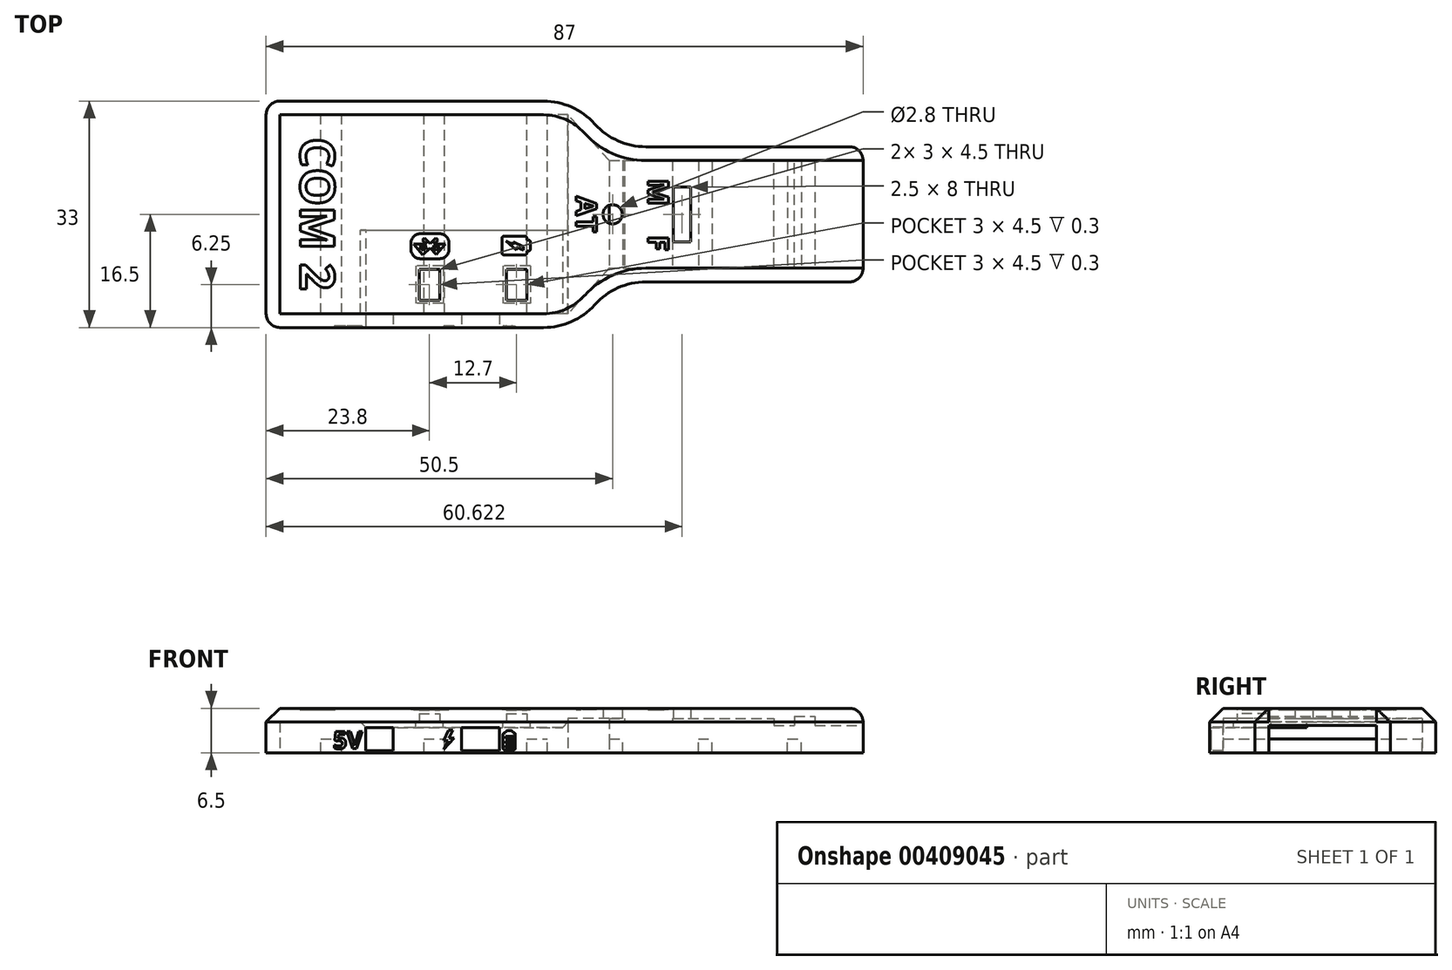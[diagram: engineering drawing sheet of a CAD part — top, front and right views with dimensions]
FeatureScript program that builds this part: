
annotation { "Feature Type Name" : "Feature", "Feature Type Description" : "" }
export const myFeature = defineFeature(function(context is Context, id is Id, definition is map)
    precondition{}
    {
        {
            var Q0;
            Q0=qCreatedBy(makeId("Top.planeOp"),FACE);
            var sketch = newSketch(context, id + "F0", { "sketchPlane" : qUnion([Q0])});
            skLineSegment(sketch, "E0.bottom", {"start": v(0, 14.5) * mm, "end": v(-42, 14.5) * mm});
            skLineSegment(sketch, "E0.top", {"start": v(0, -14.5) * mm, "end": v(-42, -14.5) * mm});
            skLineSegment(sketch, "E0.left", {"start": v(0, 14.5) * mm, "end": v(0, -14.5) * mm});
            skLineSegment(sketch, "E0.right", {"start": v(-42, 14.5) * mm, "end": v(-42, -14.5) * mm});
            skLineSegment(sketch, "E1.bottom", {"start": v(6, 7.85) * mm, "end": v(41, 7.85) * mm});
            skLineSegment(sketch, "E1.top", {"start": v(6, -7.85) * mm, "end": v(41, -7.85) * mm});
            skLineSegment(sketch, "E1.left", {"start": v(6, 7.85) * mm, "end": v(6, -7.85) * mm});
            skLineSegment(sketch, "E1.right", {"start": v(41, 7.85) * mm, "end": v(41, -7.85) * mm});
            skLineSegment(sketch, "E2", {"start": v(6, 7.85) * mm, "end": v(0, 14.5) * mm});
            skLineSegment(sketch, "E3", {"start": v(6, -7.85) * mm, "end": v(0, -14.5) * mm});
            skCircle(sketch, "E4", {"center": v(6.5, 0) * mm, "radius": 1.4 * mm});
            skLineSegment(sketch, "E5.bottom", {"start": v(-29.5, -14.5) * mm, "end": v(-25.5, -14.5) * mm});
            skLineSegment(sketch, "E5.top", {"start": v(-29.5, -17) * mm, "end": v(-25.5, -17) * mm});
            skLineSegment(sketch, "E5.left", {"start": v(-29.5, -14.5) * mm, "end": v(-29.5, -17) * mm});
            skLineSegment(sketch, "E5.right", {"start": v(-25.5, -14.5) * mm, "end": v(-25.5, -17) * mm});
            skLineSegment(sketch, "E6.bottom", {"start": v(-15.5, -14.5) * mm, "end": v(-10, -14.5) * mm});
            skLineSegment(sketch, "E6.top", {"start": v(-15.5, -17) * mm, "end": v(-10, -17) * mm});
            skLineSegment(sketch, "E6.left", {"start": v(-15.5, -14.5) * mm, "end": v(-15.5, -17) * mm});
            skLineSegment(sketch, "E6.right", {"start": v(-10, -14.5) * mm, "end": v(-10, -17) * mm});
            skLineSegment(sketch, "E7.bottom", {"start": v(-21.2, -8.5) * mm, "end": v(-19.2, -8.5) * mm});
            skLineSegment(sketch, "E7.top", {"start": v(-21.2, -12) * mm, "end": v(-19.2, -12) * mm});
            skLineSegment(sketch, "E7.left", {"start": v(-21.2, -8.5) * mm, "end": v(-21.2, -12) * mm});
            skLineSegment(sketch, "E7.right", {"start": v(-19.2, -8.5) * mm, "end": v(-19.2, -12) * mm});
            skLineSegment(sketch, "E8.bottom", {"start": v(-8.5, -8.5) * mm, "end": v(-6.5, -8.5) * mm});
            skLineSegment(sketch, "E8.top", {"start": v(-8.5, -12) * mm, "end": v(-6.5, -12) * mm});
            skLineSegment(sketch, "E8.left", {"start": v(-8.5, -8.5) * mm, "end": v(-8.5, -12) * mm});
            skLineSegment(sketch, "E8.right", {"start": v(-6.5, -8.5) * mm, "end": v(-6.5, -12) * mm});
            skLineSegment(sketch, "E9.bottom", {"start": v(-24.5, -14.5) * mm, "end": v(-30.5, -14.5) * mm});
            skLineSegment(sketch, "E9.top", {"start": v(-24.5, -9.5) * mm, "end": v(-30.5, -9.5) * mm});
            skLineSegment(sketch, "E9.left", {"start": v(-24.5, -14.5) * mm, "end": v(-24.5, -9.5) * mm});
            skLineSegment(sketch, "E9.right", {"start": v(-30.5, -14.5) * mm, "end": v(-30.5, -9.5) * mm});
            skLineSegment(sketch, "E10.bottom", {"start": v(-20, -14.5) * mm, "end": v(-7.5, -14.5) * mm});
            skLineSegment(sketch, "E10.top", {"start": v(-20, -13) * mm, "end": v(-7, -13) * mm});
            skLineSegment(sketch, "E10.left", {"start": v(-20, -14.5) * mm, "end": v(-20, -13) * mm});
            skLineSegment(sketch, "E10.right", {"start": v(-7, -14.5) * mm, "end": v(-7, -13) * mm});
            skLineSegment(sketch, "E11.bottom", {"start": v(8.2, -7.85) * mm, "end": v(15.2, -7.85) * mm});
            skLineSegment(sketch, "E11.top", {"start": v(8.2, 7.85) * mm, "end": v(15.2, 7.85) * mm});
            skLineSegment(sketch, "E11.left", {"start": v(8.2, -7.85) * mm, "end": v(8.2, 7.85) * mm});
            skLineSegment(sketch, "E11.right", {"start": v(15.2, -7.85) * mm, "end": v(15.2, 7.85) * mm});
            skLineSegment(sketch, "E12.bottom", {"start": v(17.87, 4) * mm, "end": v(15.37, 4) * mm});
            skLineSegment(sketch, "E12.top", {"start": v(17.87, -4) * mm, "end": v(15.37, -4) * mm});
            skLineSegment(sketch, "E12.left", {"start": v(17.87, 4) * mm, "end": v(17.87, -4) * mm});
            skLineSegment(sketch, "E12.right", {"start": v(15.37, 4) * mm, "end": v(15.37, -4) * mm});
            skPoint(sketch, "E12.middle", {"position": v(16.62, 0) * mm});
            skLineSegment(sketch, "E13", {"start": v(19, -8) * mm, "end": v(19, 8) * mm});
            skLineSegment(sketch, "E14", {"start": v(30, -7.85) * mm, "end": v(30, 7.85) * mm});
            skLineSegment(sketch, "E15", {"start": v(36, -7.85) * mm, "end": v(36, 7.85) * mm});
            skLineSegment(sketch, "E16", {"start": v(33, -7.85) * mm, "end": v(33, 7.85) * mm});
            skLineSegment(sketch, "E17.0", {"start": v(-9, -12.5) * mm, "end": v(-6, -12.5) * mm});
            skLineSegment(sketch, "E17.1", {"start": v(-9, -8) * mm, "end": v(-9, -12.5) * mm});
            skLineSegment(sketch, "E17.2", {"start": v(-9, -8) * mm, "end": v(-6, -8) * mm});
            skLineSegment(sketch, "E17.3", {"start": v(-6, -8) * mm, "end": v(-6, -12.5) * mm});
            skLineSegment(sketch, "E18.0", {"start": v(-21.7, -12.5) * mm, "end": v(-18.7, -12.5) * mm});
            skLineSegment(sketch, "E18.1", {"start": v(-21.7, -8) * mm, "end": v(-21.7, -12.5) * mm});
            skLineSegment(sketch, "E18.2", {"start": v(-21.7, -8) * mm, "end": v(-18.7, -8) * mm});
            skLineSegment(sketch, "E18.3", {"start": v(-18.7, -8) * mm, "end": v(-18.7, -12.5) * mm});
            skSolve(sketch);
        }
        {
            var Q0;
            Q0=makeQuery(id+"F0.imprint","IMPRINT",FACE,{"disambiguationData":[TD([[makeQuery(id+"F0.imprint","IMPRINT",EDGE,{"derivedFrom":sQuery(id+"F0.wireOp",EDGE,"E0.bottom")}),1.0]])]});
            var Q1;
            Q1=makeQuery(id+"F0.imprint","IMPRINT",FACE,{"disambiguationData":[TD([[makeQuery(id+"F0.imprint","IMPRINT",EDGE,{"derivedFrom":sQuery(id+"F0.wireOp",EDGE,"E9.top")}),1.0]])]});
            var Q2;
            {var subQ0=sQuery(id+"F0.wireOp",EDGE,"E3");Q2=makeQuery(id+"F0.imprint","IMPRINT",FACE,{"disambiguationData":[TD([[makeQuery(id+"F0.imprint","IMPRINT",EDGE,{"derivedFrom":subQ0}),-1.0]])]});}
            var Q3;
            {var subQ0=sQuery(id+"F0.wireOp",EDGE,"E2");Q3=makeQuery(id+"F0.imprint","IMPRINT",FACE,{"disambiguationData":[TD([[makeQuery(id+"F0.imprint","IMPRINT",EDGE,{"derivedFrom":subQ0}),1.0]])]});}
            var Q4;
            Q4=makeQuery(id+"F0.imprint","IMPRINT",FACE,{"disambiguationData":[TD([[makeQuery(id+"F0.imprint","IMPRINT",EDGE,{"derivedFrom":sQuery(id+"F0.wireOp",EDGE,"E10.top")}),-1.0]])]});
            var Q5;
            Q5=makeQuery(id+"F0.imprint","IMPRINT",FACE,{"disambiguationData":[TD([[makeQuery(id+"F0.imprint","IMPRINT",EDGE,{"derivedFrom":sQuery(id+"F0.wireOp",EDGE,"E7.bottom")}),-1.0]])]});
            var Q6;
            Q6=makeQuery(id+"F0.imprint","IMPRINT",FACE,{"disambiguationData":[TD([[makeQuery(id+"F0.imprint","IMPRINT",EDGE,{"derivedFrom":sQuery(id+"F0.wireOp",EDGE,"E7.bottom")}),1.0]])]});
            var Q7;
            Q7=makeQuery(id+"F0.imprint","IMPRINT",FACE,{"disambiguationData":[TD([[makeQuery(id+"F0.imprint","IMPRINT",EDGE,{"derivedFrom":sQuery(id+"F0.wireOp",EDGE,"E8.bottom")}),1.0]])]});
            var Q8;
            Q8=makeQuery(id+"F0.imprint","IMPRINT",FACE,{"disambiguationData":[TD([[makeQuery(id+"F0.imprint","IMPRINT",EDGE,{"derivedFrom":sQuery(id+"F0.wireOp",EDGE,"E8.bottom")}),-1.0]])]});
            extrude(context, id + "F1", {"entities" : qUnion([Q0, Q1, Q2, Q3, Q4, Q5, Q6, Q7, Q8]), "depth" : 4.5 * mm});
        }
        {
            var Q0;
            {var subQ5=sQuery(id+"F0.wireOp",EDGE,"E1.bottom");Q0=makeQuery(id+"F0.imprint","IMPRINT",FACE,{"disambiguationData":[TD([[makeQuery(id+"F0.imprint","IMPRINT",EDGE,{"derivedFrom":subQ5}),-1.0]])]});}
            var Q1;
            {var subQ0=sQuery(id+"F0.wireOp",EDGE,"VPpS5lpm-IVwB-HgLS-dtKc-5THlYFBJEJTK");var subQ1=sQuery(id+"F0.wireOp",EDGE,"E1.left");var subQ2=makeQuery(id+"F0.imprint","INTERSECT",VERTEX,{"disambiguationData":[OD(0.0)],"derivedFrom":[subQ1,subQ0]});Q1=makeQuery(id+"F0.imprint","IMPRINT",FACE,{"disambiguationData":[TD([[makeQuery(id+"F0.imprint","IMPRINT",EDGE,{"disambiguationData":[TD([[subQ2,-1.0]])],"derivedFrom":subQ1}),1.0]])]});}
            var Q2;
            {var subQ0=sQuery(id+"F0.wireOp",EDGE,"E4");var subQ1=sQuery(id+"F0.wireOp",EDGE,"E1.left");var subQ2=makeQuery(id+"F0.imprint","INTERSECT",VERTEX,{"disambiguationData":[OD(0.0)],"derivedFrom":[subQ1,subQ0]});Q2=makeQuery(id+"F0.imprint","IMPRINT",FACE,{"disambiguationData":[TD([[makeQuery(id+"F0.imprint","IMPRINT",EDGE,{"disambiguationData":[TD([[subQ2,-1.0]])],"derivedFrom":subQ1}),1.0]])]});}
            var Q3;
            {var subQ0=sQuery(id+"F0.wireOp",EDGE,"E1.right");Q3=makeQuery(id+"F0.imprint","IMPRINT",FACE,{"disambiguationData":[TD([[makeQuery(id+"F0.imprint","IMPRINT",EDGE,{"derivedFrom":subQ0}),-1.0]])]});}
            var Q4;
            {var subQ1=sQuery(id+"F0.wireOp",EDGE,"E1.left");var subQ4=sQuery(id+"F0.wireOp",EDGE,"VGWTlvGl-73NF-PaTW-xvmp-lA1t04jU08i1");var subQ6=makeQuery(id+"F0.imprint","INTERSECT",VERTEX,{"disambiguationData":[OD(0.0)],"derivedFrom":[subQ1,subQ4]});Q4=makeQuery(id+"F0.imprint","IMPRINT",FACE,{"disambiguationData":[TD([[makeQuery(id+"F0.imprint","IMPRINT",EDGE,{"disambiguationData":[TD([[subQ6,-1.0]])],"derivedFrom":subQ1}),1.0]])]});}
            var Q5;
            {var subQ0=sQuery(id+"F0.wireOp",EDGE,"VGWTlvGl-73NF-PaTW-xvmp-lA1t04jU08i1");var subQ1=sQuery(id+"F0.wireOp",EDGE,"E0.left");var subQ2=makeQuery(id+"F0.imprint","INTERSECT",VERTEX,{"disambiguationData":[OD(0.0)],"derivedFrom":[subQ1,subQ0]});Q5=makeQuery(id+"F0.imprint","IMPRINT",FACE,{"disambiguationData":[TD([[makeQuery(id+"F0.imprint","IMPRINT",EDGE,{"disambiguationData":[TD([[subQ2,-1.0]])],"derivedFrom":subQ1}),-1.0]])]});}
            var Q6;
            {var subQ4=sQuery(id+"F0.wireOp",EDGE,"VGWTlvGl-73NF-PaTW-xvmp-lA1t04jU08i1");var subQ7=sQuery(id+"F0.wireOp",EDGE,"E0.left");var subQ9=makeQuery(id+"F0.imprint","INTERSECT",VERTEX,{"disambiguationData":[OD(0.0)],"derivedFrom":[subQ7,subQ4]});Q6=makeQuery(id+"F0.imprint","IMPRINT",FACE,{"disambiguationData":[TD([[makeQuery(id+"F0.imprint","IMPRINT",EDGE,{"disambiguationData":[TD([[subQ9,-1.0]])],"derivedFrom":subQ7}),1.0]])]});}
            var Q7;
            {var subQ0=sQuery(id+"F0.wireOp",EDGE,"10CGU6lO-faRA-ZIwZ-rcka-2xEhCK4ulN59");var subQ1=sQuery(id+"F0.wireOp",EDGE,"E1.left");var subQ2=makeQuery(id+"F0.imprint","INTERSECT",VERTEX,{"disambiguationData":[OD(0.0)],"derivedFrom":[subQ1,subQ0]});Q7=makeQuery(id+"F0.imprint","IMPRINT",FACE,{"disambiguationData":[TD([[makeQuery(id+"F0.imprint","IMPRINT",EDGE,{"disambiguationData":[TD([[subQ2,-1.0]])],"derivedFrom":subQ1}),-1.0]])]});}
            var Q8;
            {var subQ0=sQuery(id+"F0.wireOp",EDGE,"E4");var subQ1=sQuery(id+"F0.wireOp",EDGE,"E1.left");var subQ2=makeQuery(id+"F0.imprint","INTERSECT",VERTEX,{"disambiguationData":[OD(0.0)],"derivedFrom":[subQ1,subQ0]});Q8=makeQuery(id+"F0.imprint","IMPRINT",FACE,{"disambiguationData":[TD([[makeQuery(id+"F0.imprint","IMPRINT",EDGE,{"disambiguationData":[TD([[subQ2,-1.0]])],"derivedFrom":subQ1}),-1.0]])]});}
            var Q9;
            {var subQ1=sQuery(id+"F0.wireOp",EDGE,"E1.left");var subQ3=sQuery(id+"F0.wireOp",EDGE,"10CGU6lO-faRA-ZIwZ-rcka-2xEhCK4ulN59");var subQ4=makeQuery(id+"F0.imprint","INTERSECT",VERTEX,{"disambiguationData":[OD(0.0)],"derivedFrom":[subQ1,subQ3]});Q9=makeQuery(id+"F0.imprint","IMPRINT",FACE,{"disambiguationData":[TD([[makeQuery(id+"F0.imprint","IMPRINT",EDGE,{"disambiguationData":[TD([[subQ4,1.0]])],"derivedFrom":subQ3}),-1.0]])]});}
            var Q10;
            {var subQ0=sQuery(id+"F0.wireOp",EDGE,"E11.left");var subQ1=sQuery(id+"F0.wireOp",EDGE,"10CGU6lO-faRA-ZIwZ-rcka-2xEhCK4ulN59");var subQ2=makeQuery(id+"F0.imprint","INTERSECT",VERTEX,{"disambiguationData":[OD(0.0)],"derivedFrom":[subQ1,subQ0]});Q10=makeQuery(id+"F0.imprint","IMPRINT",FACE,{"disambiguationData":[TD([[makeQuery(id+"F0.imprint","IMPRINT",EDGE,{"disambiguationData":[TD([[subQ2,1.0]])],"derivedFrom":subQ1}),-1.0]])]});}
            var Q11;
            {var subQ1=sQuery(id+"F0.wireOp",EDGE,"E11.bottom");Q11=makeQuery(id+"F0.imprint","IMPRINT",FACE,{"disambiguationData":[TD([[makeQuery(id+"F0.imprint","IMPRINT",EDGE,{"derivedFrom":subQ1}),1.0]])]});}
            var Q12;
            {var subQ1=sQuery(id+"F0.wireOp",EDGE,"E1.left");var subQ3=sQuery(id+"F0.wireOp",EDGE,"10CGU6lO-faRA-ZIwZ-rcka-2xEhCK4ulN59");var subQ4=makeQuery(id+"F0.imprint","INTERSECT",VERTEX,{"disambiguationData":[OD(1.0)],"derivedFrom":[subQ1,subQ3]});Q12=makeQuery(id+"F0.imprint","IMPRINT",FACE,{"disambiguationData":[TD([[makeQuery(id+"F0.imprint","IMPRINT",EDGE,{"disambiguationData":[TD([[subQ4,-1.0]])],"derivedFrom":subQ3}),-1.0]])]});}
            var Q13;
            {var subQ0=sQuery(id+"F0.wireOp",EDGE,"10CGU6lO-faRA-ZIwZ-rcka-2xEhCK4ulN59");var subQ1=sQuery(id+"F0.wireOp",EDGE,"E1.left");var subQ2=makeQuery(id+"F0.imprint","INTERSECT",VERTEX,{"disambiguationData":[OD(0.0)],"derivedFrom":[subQ1,subQ0]});Q13=makeQuery(id+"F0.imprint","IMPRINT",FACE,{"disambiguationData":[TD([[makeQuery(id+"F0.imprint","IMPRINT",EDGE,{"disambiguationData":[TD([[subQ2,-1.0]])],"derivedFrom":subQ1}),1.0]])]});}
            var Q14;
            {var subQ0=sQuery(id+"F0.wireOp",EDGE,"E11.left");var subQ1=sQuery(id+"F0.wireOp",EDGE,"10CGU6lO-faRA-ZIwZ-rcka-2xEhCK4ulN59");var subQ2=makeQuery(id+"F0.imprint","INTERSECT",VERTEX,{"disambiguationData":[OD(0.0)],"derivedFrom":[subQ1,subQ0]});Q14=makeQuery(id+"F0.imprint","IMPRINT",FACE,{"disambiguationData":[TD([[makeQuery(id+"F0.imprint","IMPRINT",EDGE,{"disambiguationData":[TD([[subQ2,1.0]])],"derivedFrom":subQ1}),1.0]])]});}
            var Q15;
            {var subQ0=sQuery(id+"F0.wireOp",EDGE,"HnFFDSZL-4jIR-ZRKm-03Gk-MsSLVKgGCAKZ");var subQ3=sQuery(id+"F0.wireOp",EDGE,"E11.left");var subQ5=makeQuery(id+"F0.imprint","INTERSECT",VERTEX,{"disambiguationData":[OD(1.0)],"derivedFrom":[subQ0,subQ3]});Q15=makeQuery(id+"F0.imprint","IMPRINT",FACE,{"disambiguationData":[TD([[makeQuery(id+"F0.imprint","IMPRINT",EDGE,{"disambiguationData":[TD([[subQ5,1.0]])],"derivedFrom":subQ3}),1.0]])]});}
            var Q16;
            {var subQ5=sQuery(id+"F0.wireOp",EDGE,"E12.left");Q16=makeQuery(id+"F0.imprint","IMPRINT",FACE,{"disambiguationData":[TD([[makeQuery(id+"F0.imprint","IMPRINT",EDGE,{"derivedFrom":subQ5}),-1.0]])]});}
            var Q17;
            {var subQ5=sQuery(id+"F0.wireOp",EDGE,"E12.right");Q17=makeQuery(id+"F0.imprint","IMPRINT",FACE,{"disambiguationData":[TD([[makeQuery(id+"F0.imprint","IMPRINT",EDGE,{"derivedFrom":subQ5}),1.0]])]});}
            var Q18;
            {var subQ10=sQuery(id+"F0.wireOp",EDGE,"E12.left");Q18=makeQuery(id+"F0.imprint","IMPRINT",FACE,{"disambiguationData":[TD([[makeQuery(id+"F0.imprint","IMPRINT",EDGE,{"derivedFrom":subQ10}),1.0]])]});}
            var Q19;
            {var subQ0=sQuery(id+"F0.wireOp",EDGE,"E13");Q19=makeQuery(id+"F0.imprint","IMPRINT",FACE,{"disambiguationData":[TD([[makeQuery(id+"F0.imprint","IMPRINT",EDGE,{"derivedFrom":subQ0}),-1.0]])]});}
            var Q20;
            {var subQ0=sQuery(id+"F0.wireOp",EDGE,"E14");Q20=makeQuery(id+"F0.imprint","IMPRINT",FACE,{"disambiguationData":[TD([[makeQuery(id+"F0.imprint","IMPRINT",EDGE,{"derivedFrom":subQ0}),-1.0]])]});}
            var Q21;
            {var subQ0=sQuery(id+"F0.wireOp",EDGE,"E15");Q21=makeQuery(id+"F0.imprint","IMPRINT",FACE,{"disambiguationData":[TD([[makeQuery(id+"F0.imprint","IMPRINT",EDGE,{"derivedFrom":subQ0}),1.0]])]});}
            extrude(context, id + "F2", {"entities" : qUnion([Q0, Q1, Q2, Q3, Q4, Q5, Q6, Q7, Q8, Q9, Q10, Q11, Q12, Q13, Q14, Q15, Q16, Q17, Q18, Q19, Q20, Q21]), "depth" : 4.5 * mm});
        }
        {
            var Q0;
            {var subQ0=sQuery(id+"F0.wireOp",EDGE,"VPpS5lpm-IVwB-HgLS-dtKc-5THlYFBJEJTK");var subQ2=sQuery(id+"F0.wireOp",EDGE,"E1.left");var subQ3=makeQuery(id+"F0.imprint","INTERSECT",VERTEX,{"disambiguationData":[OD(0.0)],"derivedFrom":[subQ2,subQ0]});Q0=makeQuery(id+"F0.imprint","IMPRINT",FACE,{"disambiguationData":[TD([[makeQuery(id+"F0.imprint","IMPRINT",EDGE,{"disambiguationData":[TD([[subQ3,-1.0]])],"derivedFrom":subQ2}),-1.0]])]});}
            var Q1;
            {var subQ0=sQuery(id+"F0.wireOp",EDGE,"y9EbTcyz-21YZ-qjv3-pbne-yzflViiAGyzZ");Q1=makeQuery(id+"F0.imprint","IMPRINT",FACE,{"disambiguationData":[TD([[makeQuery(id+"F0.imprint","IMPRINT",EDGE,{"derivedFrom":subQ0}),-1.0]])]});}
            var Q2;
            {var subQ0=sQuery(id+"F0.wireOp",EDGE,"10CGU6lO-faRA-ZIwZ-rcka-2xEhCK4ulN59");var subQ1=sQuery(id+"F0.wireOp",EDGE,"E1.left");var subQ2=makeQuery(id+"F0.imprint","INTERSECT",VERTEX,{"disambiguationData":[OD(0.0)],"derivedFrom":[subQ1,subQ0]});Q2=makeQuery(id+"F0.imprint","IMPRINT",FACE,{"disambiguationData":[TD([[makeQuery(id+"F0.imprint","IMPRINT",EDGE,{"disambiguationData":[TD([[subQ2,-1.0]])],"derivedFrom":subQ1}),-1.0]])]});}
            var Q3;
            {var subQ4=sQuery(id+"F0.wireOp",EDGE,"VGWTlvGl-73NF-PaTW-xvmp-lA1t04jU08i1");var subQ7=sQuery(id+"F0.wireOp",EDGE,"E0.left");var subQ9=makeQuery(id+"F0.imprint","INTERSECT",VERTEX,{"disambiguationData":[OD(0.0)],"derivedFrom":[subQ7,subQ4]});Q3=makeQuery(id+"F0.imprint","IMPRINT",FACE,{"disambiguationData":[TD([[makeQuery(id+"F0.imprint","IMPRINT",EDGE,{"disambiguationData":[TD([[subQ9,-1.0]])],"derivedFrom":subQ7}),1.0]])]});}
            var Q4;
            {var subQ0=sQuery(id+"F0.wireOp",EDGE,"VGWTlvGl-73NF-PaTW-xvmp-lA1t04jU08i1");var subQ1=sQuery(id+"F0.wireOp",EDGE,"E0.left");var subQ2=makeQuery(id+"F0.imprint","INTERSECT",VERTEX,{"disambiguationData":[OD(0.0)],"derivedFrom":[subQ1,subQ0]});Q4=makeQuery(id+"F0.imprint","IMPRINT",FACE,{"disambiguationData":[TD([[makeQuery(id+"F0.imprint","IMPRINT",EDGE,{"disambiguationData":[TD([[subQ2,-1.0]])],"derivedFrom":subQ1}),-1.0]])]});}
            extrude(context, id + "F3", {"entities" : qUnion([Q0, Q1, Q2, Q3, Q4]), "depth" : 4.5 * mm});
        }
        {
            var Q0;
            Q0=makeQuery(id+"F1.opExtrude","SWEPT_BODY",BODY,{"disambiguationData":[OSD([sQuery(id+"F0.wireOp",EDGE,"E0.bottom"),sQuery(id+"F0.wireOp",EDGE,"E0.top"),sQuery(id+"F0.wireOp",EDGE,"E0.right"),sQuery(id+"F0.wireOp",EDGE,"E1.left"),sQuery(id+"F0.wireOp",EDGE,"E2"),sQuery(id+"F0.wireOp",EDGE,"E3"),sQuery(id+"F0.wireOp",EDGE,"E6.bottom"),sQuery(id+"F0.wireOp",EDGE,"E9.bottom"),sQuery(id+"F0.wireOp",EDGE,"VGWTlvGl-73NF-PaTW-xvmp-lA1t04jU08i1")])]});
            var Q1;
            Q1=makeQuery(id+"F2.opExtrude","SWEPT_BODY",BODY,{"disambiguationData":[OSD([sQuery(id+"F0.wireOp",EDGE,"E1.bottom"),sQuery(id+"F0.wireOp",EDGE,"E1.top"),sQuery(id+"F0.wireOp",EDGE,"E1.left"),sQuery(id+"F0.wireOp",EDGE,"E1.right"),sQuery(id+"F0.wireOp",EDGE,"VGWTlvGl-73NF-PaTW-xvmp-lA1t04jU08i1")])]});
            var Q2;
            Q2=makeQuery(id+"F3.opExtrude","SWEPT_BODY",BODY,{"disambiguationData":[OSD([sQuery(id+"F0.wireOp",EDGE,"E1.left"),sQuery(id+"F0.wireOp",EDGE,"E4"),sQuery(id+"F0.wireOp",EDGE,"VGWTlvGl-73NF-PaTW-xvmp-lA1t04jU08i1")])]});
            booleanBodies(context, id + "F4", {"operationType" : BooleanOperationType.UNION, "tools" : qUnion([Q0, Q1, Q2])});
        }
        {
            var Q0;
            {var subQ0=sQuery(id+"F0.wireOp",EDGE,"VGWTlvGl-73NF-PaTW-xvmp-lA1t04jU08i1");var subQ1=sQuery(id+"F0.wireOp",EDGE,"E1.left");Q0=makeQuery(id+"F4.opBoolean","MERGE",FACE,{"derivedFrom":[makeQuery(id+"F1.opExtrude","CAP_FACE",FACE,{"disambiguationData":[OSD([sQuery(id+"F0.wireOp",EDGE,"E0.bottom"),sQuery(id+"F0.wireOp",EDGE,"E0.top"),sQuery(id+"F0.wireOp",EDGE,"E0.right"),subQ1,sQuery(id+"F0.wireOp",EDGE,"E2"),sQuery(id+"F0.wireOp",EDGE,"E3"),sQuery(id+"F0.wireOp",EDGE,"E6.bottom"),sQuery(id+"F0.wireOp",EDGE,"E9.bottom"),subQ0])],"isStart":true}),makeQuery(id+"F2.opExtrude","CAP_FACE",FACE,{"disambiguationData":[OSD([sQuery(id+"F0.wireOp",EDGE,"E1.bottom"),sQuery(id+"F0.wireOp",EDGE,"E1.top"),subQ1,sQuery(id+"F0.wireOp",EDGE,"E1.right"),subQ0])],"isStart":true})]});}
            shell(context, id + "F5", {"entities" : qUnion([Q0]), "thickness" : 2 * mm, "oppositeDirection" : true});
        }
        {
            var Q0;
            {var subQ0=sQuery(id+"F0.wireOp",EDGE,"E4");var subQ1=sQuery(id+"F0.wireOp",EDGE,"E1.left");var subQ2=makeQuery(id+"F0.imprint","INTERSECT",VERTEX,{"disambiguationData":[OD(0.0)],"derivedFrom":[subQ1,subQ0]});Q0=makeQuery(id+"F0.imprint","IMPRINT",FACE,{"disambiguationData":[TD([[makeQuery(id+"F0.imprint","IMPRINT",EDGE,{"disambiguationData":[TD([[subQ2,-1.0]])],"derivedFrom":subQ1}),1.0]])]});}
            var Q1;
            {var subQ0=sQuery(id+"F0.wireOp",EDGE,"E4");var subQ1=sQuery(id+"F0.wireOp",EDGE,"E1.left");var subQ2=makeQuery(id+"F0.imprint","INTERSECT",VERTEX,{"disambiguationData":[OD(0.0)],"derivedFrom":[subQ1,subQ0]});Q1=makeQuery(id+"F0.imprint","IMPRINT",FACE,{"disambiguationData":[TD([[makeQuery(id+"F0.imprint","IMPRINT",EDGE,{"disambiguationData":[TD([[subQ2,-1.0]])],"derivedFrom":subQ1}),-1.0]])]});}
            extrude(context, id + "F6", {"entities" : qUnion([Q0, Q1]), "operationType" : NewBodyOperationType.REMOVE, "depth" : 25 * mm});
        }
        {
            var Q0;
            Q0=makeQuery(id+"F0.imprint","IMPRINT",FACE,{"disambiguationData":[TD([[makeQuery(id+"F0.imprint","IMPRINT",EDGE,{"derivedFrom":sQuery(id+"F0.wireOp",EDGE,"E5.top")}),1.0]])]});
            var Q1;
            Q1=makeQuery(id+"F0.imprint","IMPRINT",FACE,{"disambiguationData":[TD([[makeQuery(id+"F0.imprint","IMPRINT",EDGE,{"derivedFrom":sQuery(id+"F0.wireOp",EDGE,"E6.bottom")}),-1.0]])]});
            var Q2;
            Q2=makeQuery(id+"F0.imprint","IMPRINT",FACE,{"disambiguationData":[TD([[makeQuery(id+"F0.imprint","IMPRINT",EDGE,{"derivedFrom":sQuery(id+"F0.wireOp",EDGE,"E9.top")}),1.0]])]});
            var Q3;
            Q3=makeQuery(id+"F0.imprint","IMPRINT",FACE,{"disambiguationData":[TD([[makeQuery(id+"F0.imprint","IMPRINT",EDGE,{"derivedFrom":sQuery(id+"F0.wireOp",EDGE,"E10.top")}),-1.0]])]});
            var Q4;
            Q4=makeQuery(id+"F0.imprint","IMPRINT",FACE,{"disambiguationData":[TD([[makeQuery(id+"F0.imprint","IMPRINT",EDGE,{"derivedFrom":sQuery(id+"F0.wireOp",EDGE,"E6.top")}),1.0]])]});
            extrude(context, id + "F7", {"entities" : qUnion([Q0, Q1, Q2, Q3, Q4]), "operationType" : NewBodyOperationType.REMOVE, "depth" : 4 * mm});
        }
        {
            var Q0;
            {var subQ0=sQuery(id+"F0.wireOp",EDGE,"HnFFDSZL-4jIR-ZRKm-03Gk-MsSLVKgGCAKZ");var subQ1=sQuery(id+"F0.wireOp",EDGE,"E3");var subQ2=sQuery(id+"F0.wireOp",EDGE,"E1.left");var subQ3=sQuery(id+"F0.wireOp",EDGE,"E1.top");Q0=makeQuery(id+"F4.opBoolean","MERGE",EDGE,{"derivedFrom":[makeQuery(id+"F1.opExtrude","SWEPT_EDGE",EDGE,{"disambiguationData":[OSD([subQ3,subQ2,subQ1,subQ0])]}),makeQuery(id+"F2.opExtrude","SWEPT_EDGE",EDGE,{"disambiguationData":[OSD([subQ3,subQ2,subQ1,subQ0])]})]});}
            var Q1;
            Q1=makeQuery(id+"F1.opExtrude","SWEPT_EDGE",EDGE,{"disambiguationData":[OSD([sQuery(id+"F0.wireOp",EDGE,"E0.top"),sQuery(id+"F0.wireOp",EDGE,"E0.left"),sQuery(id+"F0.wireOp",EDGE,"E3")])]});
            var Q2;
            {var subQ0=sQuery(id+"F0.wireOp",EDGE,"HnFFDSZL-4jIR-ZRKm-03Gk-MsSLVKgGCAKZ");var subQ1=sQuery(id+"F0.wireOp",EDGE,"E2");var subQ2=sQuery(id+"F0.wireOp",EDGE,"E1.left");var subQ3=sQuery(id+"F0.wireOp",EDGE,"E1.bottom");Q2=makeQuery(id+"F4.opBoolean","MERGE",EDGE,{"derivedFrom":[makeQuery(id+"F1.opExtrude","SWEPT_EDGE",EDGE,{"disambiguationData":[OSD([subQ3,subQ2,subQ1,subQ0])]}),makeQuery(id+"F2.opExtrude","SWEPT_EDGE",EDGE,{"disambiguationData":[OSD([subQ3,subQ2,subQ1,subQ0])]})]});}
            var Q3;
            Q3=makeQuery(id+"F1.opExtrude","SWEPT_EDGE",EDGE,{"disambiguationData":[OSD([sQuery(id+"F0.wireOp",EDGE,"E0.bottom"),sQuery(id+"F0.wireOp",EDGE,"E0.left"),sQuery(id+"F0.wireOp",EDGE,"E2")])]});
            fillet(context, id + "F8", {"entities" : qUnion([Q0, Q1, Q2, Q3]), "radius" : 10 * mm, "tangentPropagation" : true, "allowEdgeOverflow" : false});
        }
        {
            var Q0;
            Q0=makeQuery(id+"F5.opShell","OFFSET_FACE",FACE,{"disambiguationData":[OSD([sQuery(id+"F0.wireOp",EDGE,"E1.right")])]});
            extrude(context, id + "F9", {"entities" : qUnion([Q0]), "operationType" : NewBodyOperationType.REMOVE, "oppositeDirection" : true, "depth" : 25 * mm});
        }
        {
            var Q0;
            Q0=makeQuery(id+"F1.opExtrude","SWEPT_EDGE",EDGE,{"disambiguationData":[OSD([sQuery(id+"F0.wireOp",EDGE,"E0.bottom"),sQuery(id+"F0.wireOp",EDGE,"E0.right")])]});
            var Q1;
            Q1=makeQuery(id+"F1.opExtrude","SWEPT_EDGE",EDGE,{"disambiguationData":[OSD([sQuery(id+"F0.wireOp",EDGE,"E0.top"),sQuery(id+"F0.wireOp",EDGE,"E0.right")])]});
            fillet(context, id + "F10", {"entities" : qUnion([Q0, Q1]), "radius" : 2 * mm, "tangentPropagation" : true, "allowEdgeOverflow" : false});
        }
        {
            var Q0;
            {var subQ0=sQuery(id+"F0.wireOp",EDGE,"HnFFDSZL-4jIR-ZRKm-03Gk-MsSLVKgGCAKZ");var subQ7=sQuery(id+"F0.wireOp",EDGE,"E0.left");var subQ8=makeQuery(id+"F0.imprint","INTERSECT",VERTEX,{"disambiguationData":[OD(0.0)],"derivedFrom":[subQ7,subQ0]});Q0=makeQuery(id+"F0.imprint","IMPRINT",FACE,{"disambiguationData":[TD([[makeQuery(id+"F0.imprint","IMPRINT",EDGE,{"disambiguationData":[TD([[subQ8,-1.0]])],"derivedFrom":subQ7}),1.0]])]});}
            var Q1;
            {var subQ0=sQuery(id+"F0.wireOp",EDGE,"10CGU6lO-faRA-ZIwZ-rcka-2xEhCK4ulN59");var subQ1=sQuery(id+"F0.wireOp",EDGE,"E1.left");var subQ2=makeQuery(id+"F0.imprint","INTERSECT",VERTEX,{"disambiguationData":[OD(0.0)],"derivedFrom":[subQ1,subQ0]});Q1=makeQuery(id+"F0.imprint","IMPRINT",FACE,{"disambiguationData":[TD([[makeQuery(id+"F0.imprint","IMPRINT",EDGE,{"disambiguationData":[TD([[subQ2,-1.0]])],"derivedFrom":subQ1}),-1.0]])]});}
            var Q2;
            {var subQ0=sQuery(id+"F0.wireOp",EDGE,"10CGU6lO-faRA-ZIwZ-rcka-2xEhCK4ulN59");var subQ1=sQuery(id+"F0.wireOp",EDGE,"E1.left");var subQ2=makeQuery(id+"F0.imprint","INTERSECT",VERTEX,{"disambiguationData":[OD(0.0)],"derivedFrom":[subQ1,subQ0]});Q2=makeQuery(id+"F0.imprint","IMPRINT",FACE,{"disambiguationData":[TD([[makeQuery(id+"F0.imprint","IMPRINT",EDGE,{"disambiguationData":[TD([[subQ2,-1.0]])],"derivedFrom":subQ1}),1.0]])]});}
            var Q3;
            {var subQ1=sQuery(id+"F0.wireOp",EDGE,"E1.left");var subQ3=sQuery(id+"F0.wireOp",EDGE,"10CGU6lO-faRA-ZIwZ-rcka-2xEhCK4ulN59");var subQ4=makeQuery(id+"F0.imprint","INTERSECT",VERTEX,{"disambiguationData":[OD(0.0)],"derivedFrom":[subQ1,subQ3]});Q3=makeQuery(id+"F0.imprint","IMPRINT",FACE,{"disambiguationData":[TD([[makeQuery(id+"F0.imprint","IMPRINT",EDGE,{"disambiguationData":[TD([[subQ4,1.0]])],"derivedFrom":subQ3}),-1.0]])]});}
            var Q4;
            {var subQ1=sQuery(id+"F0.wireOp",EDGE,"E1.left");var subQ3=sQuery(id+"F0.wireOp",EDGE,"10CGU6lO-faRA-ZIwZ-rcka-2xEhCK4ulN59");var subQ4=makeQuery(id+"F0.imprint","INTERSECT",VERTEX,{"disambiguationData":[OD(1.0)],"derivedFrom":[subQ1,subQ3]});Q4=makeQuery(id+"F0.imprint","IMPRINT",FACE,{"disambiguationData":[TD([[makeQuery(id+"F0.imprint","IMPRINT",EDGE,{"disambiguationData":[TD([[subQ4,-1.0]])],"derivedFrom":subQ3}),-1.0]])]});}
            var Q5;
            {var subQ0=sQuery(id+"F0.wireOp",EDGE,"E11.left");var subQ1=sQuery(id+"F0.wireOp",EDGE,"10CGU6lO-faRA-ZIwZ-rcka-2xEhCK4ulN59");var subQ2=makeQuery(id+"F0.imprint","INTERSECT",VERTEX,{"disambiguationData":[OD(0.0)],"derivedFrom":[subQ1,subQ0]});Q5=makeQuery(id+"F0.imprint","IMPRINT",FACE,{"disambiguationData":[TD([[makeQuery(id+"F0.imprint","IMPRINT",EDGE,{"disambiguationData":[TD([[subQ2,1.0]])],"derivedFrom":subQ1}),1.0]])]});}
            var Q6;
            {var subQ0=sQuery(id+"F0.wireOp",EDGE,"E11.left");var subQ1=sQuery(id+"F0.wireOp",EDGE,"10CGU6lO-faRA-ZIwZ-rcka-2xEhCK4ulN59");var subQ2=makeQuery(id+"F0.imprint","INTERSECT",VERTEX,{"disambiguationData":[OD(0.0)],"derivedFrom":[subQ1,subQ0]});Q6=makeQuery(id+"F0.imprint","IMPRINT",FACE,{"disambiguationData":[TD([[makeQuery(id+"F0.imprint","IMPRINT",EDGE,{"disambiguationData":[TD([[subQ2,1.0]])],"derivedFrom":subQ1}),-1.0]])]});}
            extrude(context, id + "F11", {"entities" : qUnion([Q0, Q1, Q2, Q3, Q4, Q5, Q6]), "operationType" : NewBodyOperationType.REMOVE, "depth" : 5 * mm});
        }
        {
            var Q0;
            {var subQ0=sQuery(id+"F0.wireOp",EDGE,"E11.left");var subQ1=sQuery(id+"F0.wireOp",EDGE,"10CGU6lO-faRA-ZIwZ-rcka-2xEhCK4ulN59");var subQ2=makeQuery(id+"F0.imprint","INTERSECT",VERTEX,{"disambiguationData":[OD(0.0)],"derivedFrom":[subQ1,subQ0]});Q0=makeQuery(id+"F0.imprint","IMPRINT",FACE,{"disambiguationData":[TD([[makeQuery(id+"F0.imprint","IMPRINT",EDGE,{"disambiguationData":[TD([[subQ2,1.0]])],"derivedFrom":subQ1}),1.0]])]});}
            var Q1;
            {var subQ10=sQuery(id+"F0.wireOp",EDGE,"E12.left");Q1=makeQuery(id+"F0.imprint","IMPRINT",FACE,{"disambiguationData":[TD([[makeQuery(id+"F0.imprint","IMPRINT",EDGE,{"derivedFrom":subQ10}),1.0]])]});}
            var Q2;
            {var subQ1=sQuery(id+"F0.wireOp",EDGE,"E11.bottom");Q2=makeQuery(id+"F0.imprint","IMPRINT",FACE,{"disambiguationData":[TD([[makeQuery(id+"F0.imprint","IMPRINT",EDGE,{"derivedFrom":subQ1}),1.0]])]});}
            var Q3;
            {var subQ5=sQuery(id+"F0.wireOp",EDGE,"E12.right");Q3=makeQuery(id+"F0.imprint","IMPRINT",FACE,{"disambiguationData":[TD([[makeQuery(id+"F0.imprint","IMPRINT",EDGE,{"derivedFrom":subQ5}),1.0]])]});}
            var Q4;
            {var subQ0=sQuery(id+"F0.wireOp",EDGE,"HnFFDSZL-4jIR-ZRKm-03Gk-MsSLVKgGCAKZ");var subQ3=sQuery(id+"F0.wireOp",EDGE,"E11.left");var subQ5=makeQuery(id+"F0.imprint","INTERSECT",VERTEX,{"disambiguationData":[OD(1.0)],"derivedFrom":[subQ0,subQ3]});Q4=makeQuery(id+"F0.imprint","IMPRINT",FACE,{"disambiguationData":[TD([[makeQuery(id+"F0.imprint","IMPRINT",EDGE,{"disambiguationData":[TD([[subQ5,1.0]])],"derivedFrom":subQ3}),1.0]])]});}
            var Q5;
            {var subQ0=sQuery(id+"F0.wireOp",EDGE,"HnFFDSZL-4jIR-ZRKm-03Gk-MsSLVKgGCAKZ");var subQ3=sQuery(id+"F0.wireOp",EDGE,"E11.left");var subQ5=makeQuery(id+"F0.imprint","INTERSECT",VERTEX,{"disambiguationData":[OD(0.0)],"derivedFrom":[subQ0,subQ3]});Q5=makeQuery(id+"F0.imprint","IMPRINT",FACE,{"disambiguationData":[TD([[makeQuery(id+"F0.imprint","IMPRINT",EDGE,{"disambiguationData":[TD([[subQ5,-1.0]])],"derivedFrom":subQ3}),1.0]])]});}
            var Q6;
            {var subQ0=sQuery(id+"F0.wireOp",EDGE,"E11.left");var subQ1=sQuery(id+"F0.wireOp",EDGE,"10CGU6lO-faRA-ZIwZ-rcka-2xEhCK4ulN59");var subQ2=makeQuery(id+"F0.imprint","INTERSECT",VERTEX,{"disambiguationData":[OD(0.0)],"derivedFrom":[subQ1,subQ0]});Q6=makeQuery(id+"F0.imprint","IMPRINT",FACE,{"disambiguationData":[TD([[makeQuery(id+"F0.imprint","IMPRINT",EDGE,{"disambiguationData":[TD([[subQ2,1.0]])],"derivedFrom":subQ1}),-1.0]])]});}
            extrude(context, id + "F12", {"entities" : qUnion([Q0, Q1, Q2, Q3, Q4, Q5, Q6]), "operationType" : NewBodyOperationType.REMOVE, "depth" : 5 * mm});
        }
        {
            var Q0;
            {var subQ5=sQuery(id+"F0.wireOp",EDGE,"E12.left");Q0=makeQuery(id+"F0.imprint","IMPRINT",FACE,{"disambiguationData":[TD([[makeQuery(id+"F0.imprint","IMPRINT",EDGE,{"derivedFrom":subQ5}),-1.0]])]});}
            extrude(context, id + "F13", {"entities" : qUnion([Q0]), "operationType" : NewBodyOperationType.REMOVE, "depth" : 25 * mm});
        }
        {
            var Q0;
            {var subQ0=sQuery(id+"F0.wireOp",EDGE,"E15");Q0=makeQuery(id+"F0.imprint","IMPRINT",FACE,{"disambiguationData":[TD([[makeQuery(id+"F0.imprint","IMPRINT",EDGE,{"derivedFrom":subQ0}),1.0]])]});}
            var Q1;
            {var subQ0=sQuery(id+"F0.wireOp",EDGE,"E13");Q1=makeQuery(id+"F0.imprint","IMPRINT",FACE,{"disambiguationData":[TD([[makeQuery(id+"F0.imprint","IMPRINT",EDGE,{"derivedFrom":subQ0}),-1.0]])]});}
            extrude(context, id + "F14", {"entities" : qUnion([Q0, Q1]), "operationType" : NewBodyOperationType.REMOVE, "depth" : 5 * mm});
        }
        {
            var Q0;
            {var subQ0=sQuery(id+"F0.wireOp",EDGE,"HnFFDSZL-4jIR-ZRKm-03Gk-MsSLVKgGCAKZ");Q0=makeQuery(id+"F4.opBoolean","MERGE",FACE,{"derivedFrom":[makeQuery(id+"F1.opExtrude","CAP_FACE",FACE,{"disambiguationData":[OSD([sQuery(id+"F0.wireOp",EDGE,"E0.bottom"),sQuery(id+"F0.wireOp",EDGE,"E0.top"),sQuery(id+"F0.wireOp",EDGE,"E0.right"),sQuery(id+"F0.wireOp",EDGE,"E2"),sQuery(id+"F0.wireOp",EDGE,"E3"),sQuery(id+"F0.wireOp",EDGE,"E9.bottom"),sQuery(id+"F0.wireOp",EDGE,"E10.bottom"),subQ0])],"isStart":false}),makeQuery(id+"F2.opExtrude","CAP_FACE",FACE,{"disambiguationData":[OSD([sQuery(id+"F0.wireOp",EDGE,"E1.bottom"),sQuery(id+"F0.wireOp",EDGE,"E1.top"),sQuery(id+"F0.wireOp",EDGE,"E1.right"),subQ0,sQuery(id+"F0.wireOp",EDGE,"E11.bottom"),sQuery(id+"F0.wireOp",EDGE,"E11.top")])],"isStart":false})]});}
            var sketch = newSketch(context, id + "F15", { "sketchPlane" : qUnion([Q0])});
            skPoint(sketch, "E19.middle", {"position": v(-19.64, -4.61) * mm});
            skLineSegment(sketch, "E20", {"start": v(-18.72, -4.71) * mm, "end": v(-19.8, -4.73) * mm});
            skLineSegment(sketch, "E21", {"start": v(-19.8, -4.73) * mm, "end": v(-19.22, -5.28) * mm});
            skLineSegment(sketch, "E22", {"start": v(-19.22, -5.28) * mm, "end": v(-18.72, -4.71) * mm});
            skLineSegment(sketch, "E23", {"start": v(-20.54, -4.76) * mm, "end": v(-21.66, -4.76) * mm});
            skLineSegment(sketch, "E24", {"start": v(-21.66, -4.76) * mm, "end": v(-21.13, -5.31) * mm});
            skLineSegment(sketch, "E25", {"start": v(-21.13, -5.31) * mm, "end": v(-20.54, -4.76) * mm});
            skLineSegment(sketch, "E26", {"start": v(-20.12, -4.91) * mm, "end": v(-21.19, -5.94) * mm});
            skLineSegment(sketch, "E27", {"start": v(-21.19, -5.94) * mm, "end": v(-22.52, -4.36) * mm});
            skLineSegment(sketch, "E28", {"start": v(-22.52, -4.36) * mm, "end": v(-20.6, -4.37) * mm});
            skLineSegment(sketch, "E29", {"start": v(-20.6, -4.37) * mm, "end": v(-21.24, -3.74) * mm});
            skLineSegment(sketch, "E30", {"start": v(-21.24, -3.74) * mm, "end": v(-20.95, -3.45) * mm});
            skLineSegment(sketch, "E31", {"start": v(-20.95, -3.45) * mm, "end": v(-20.1, -4.28) * mm});
            skLineSegment(sketch, "E32", {"start": v(-20.1, -4.28) * mm, "end": v(-19.28, -3.45) * mm});
            skLineSegment(sketch, "E33", {"start": v(-19.28, -3.45) * mm, "end": v(-18.97, -3.75) * mm});
            skLineSegment(sketch, "E34", {"start": v(-18.97, -3.75) * mm, "end": v(-19.56, -4.34) * mm});
            skLineSegment(sketch, "E35", {"start": v(-19.56, -4.34) * mm, "end": v(-17.84, -4.33) * mm});
            skLineSegment(sketch, "E36", {"start": v(-17.84, -4.33) * mm, "end": v(-19.2, -5.89) * mm});
            skLineSegment(sketch, "E37", {"start": v(-19.2, -5.89) * mm, "end": v(-20.12, -4.91) * mm});
            skText(sketch, "E38", { "text": "M    F", "fontName": "OpenSans-Bold.ttf"});
            skText(sketch, "E39", { "text": "AT", "fontName": "OpenSans-Bold.ttf"});
            skText(sketch, "E40", { "text": "COM 2", "fontName": "OpenSans-Bold.ttf"});
            skLineSegment(sketch, "E41.bottom", {"start": v(-6.24, -3.21) * mm, "end": v(-9.4, -3.21) * mm});
            skLineSegment(sketch, "E41.top", {"start": v(-6.24, -5.9) * mm, "end": v(-9.4, -5.9) * mm});
            skLineSegment(sketch, "E41.left", {"start": v(-6, -3.44) * mm, "end": v(-6, -5.66) * mm});
            skLineSegment(sketch, "E41.right", {"start": v(-9.63, -3.44) * mm, "end": v(-9.63, -5.66) * mm});
            skPoint(sketch, "E42.visualSharp", {"position": v(-6, -3.21) * mm});
            skArc(sketch, "E42.filletArc", {"start": v(-6, -3.44) * mm, "mid": v(-6.07, -3.28) * mm, "end": v(-6.24, -3.21) * mm});
            skPoint(sketch, "E43.visualSharp", {"position": v(-6, -5.9) * mm});
            skArc(sketch, "E43.filletArc", {"start": v(-6.24, -5.9) * mm, "mid": v(-6.07, -5.83) * mm, "end": v(-6, -5.66) * mm});
            skPoint(sketch, "E44.visualSharp", {"position": v(-9.63, -3.21) * mm});
            skArc(sketch, "E44.filletArc", {"start": v(-9.4, -3.21) * mm, "mid": v(-9.56, -3.28) * mm, "end": v(-9.63, -3.44) * mm});
            skPoint(sketch, "E45.visualSharp", {"position": v(-9.63, -5.9) * mm});
            skArc(sketch, "E45.filletArc", {"start": v(-9.63, -5.66) * mm, "mid": v(-9.56, -5.83) * mm, "end": v(-9.4, -5.9) * mm});
            skLineSegment(sketch, "E46.bottom", {"start": v(-6, -3.76) * mm, "end": v(-5.74, -3.76) * mm});
            skLineSegment(sketch, "E46.top", {"start": v(-6, -5.35) * mm, "end": v(-5.74, -5.35) * mm});
            skLineSegment(sketch, "E46.left", {"start": v(-6, -3.76) * mm, "end": v(-6, -5.35) * mm});
            skLineSegment(sketch, "E46.right", {"start": v(-5.5, -4) * mm, "end": v(-5.5, -5.11) * mm});
            skPoint(sketch, "E47.visualSharp", {"position": v(-5.5, -3.76) * mm});
            skArc(sketch, "E47.filletArc", {"start": v(-5.5, -4) * mm, "mid": v(-5.57, -3.83) * mm, "end": v(-5.74, -3.76) * mm});
            skPoint(sketch, "E48.visualSharp", {"position": v(-5.5, -5.35) * mm});
            skArc(sketch, "E48.filletArc", {"start": v(-5.74, -5.35) * mm, "mid": v(-5.57, -5.28) * mm, "end": v(-5.5, -5.11) * mm});
            skLineSegment(sketch, "E49", {"start": v(-6.53, -4.71) * mm, "end": v(-7.98, -4) * mm});
            skLineSegment(sketch, "E50", {"start": v(-7.98, -4) * mm, "end": v(-7.98, -4.4) * mm});
            skLineSegment(sketch, "E51", {"start": v(-7.98, -4.4) * mm, "end": v(-9.07, -3.9) * mm});
            skLineSegment(sketch, "E52", {"start": v(-9.07, -3.9) * mm, "end": v(-7.5, -5.2) * mm});
            skLineSegment(sketch, "E53", {"start": v(-7.5, -5.2) * mm, "end": v(-7.5, -4.76) * mm});
            skLineSegment(sketch, "E54", {"start": v(-7.5, -4.76) * mm, "end": v(-6.53, -5.25) * mm});
            skLineSegment(sketch, "E55", {"start": v(-6.53, -5.25) * mm, "end": v(-6.53, -4.71) * mm});
            skLineSegment(sketch, "E56.bottom", {"start": v(-21.54, -6.47) * mm, "end": v(-18.7, -6.47) * mm});
            skLineSegment(sketch, "E56.top", {"start": v(-21.54, -2.84) * mm, "end": v(-18.7, -2.84) * mm});
            skLineSegment(sketch, "E56.left", {"start": v(-22.89, -5.12) * mm, "end": v(-22.89, -4.19) * mm});
            skLineSegment(sketch, "E56.right", {"start": v(-17.35, -5.12) * mm, "end": v(-17.35, -4.19) * mm});
            skPoint(sketch, "E56.middle", {"position": v(-20.12, -4.65) * mm});
            skPoint(sketch, "E57.visualSharp", {"position": v(-17.35, -2.84) * mm});
            skArc(sketch, "E57.filletArc", {"start": v(-17.35, -4.19) * mm, "mid": v(-17.75, -3.23) * mm, "end": v(-18.7, -2.84) * mm});
            skPoint(sketch, "E58.visualSharp", {"position": v(-17.35, -6.47) * mm});
            skArc(sketch, "E58.filletArc", {"start": v(-18.7, -6.47) * mm, "mid": v(-17.75, -6.07) * mm, "end": v(-17.35, -5.12) * mm});
            skPoint(sketch, "E59.visualSharp", {"position": v(-22.89, -6.47) * mm});
            skArc(sketch, "E59.filletArc", {"start": v(-22.89, -5.12) * mm, "mid": v(-22.5, -6.07) * mm, "end": v(-21.54, -6.47) * mm});
            skPoint(sketch, "E60.visualSharp", {"position": v(-22.89, -2.84) * mm});
            skArc(sketch, "E60.filletArc", {"start": v(-21.54, -2.84) * mm, "mid": v(-22.5, -3.23) * mm, "end": v(-22.89, -4.19) * mm});
            const initialGuessF15  = {"E38": [0.01167, 0.0052, 0, -1, 0.003], "E39": [0.0012, 0.00264, 0, -1, 0.003], "E40": [-0.039, 0.0112, 0, -1, 0.005]};
            skSetInitialGuess(sketch, initialGuessF15);
            skSolve(sketch);
        }
        {
            var Q0;
            {var subQ5=sQuery(id+"F15.wireOp",EDGE,"E19.right");Q0=makeQuery(id+"F15.imprint","IMPRINT",FACE,{"disambiguationData":[TD([[makeQuery(id+"F15.imprint","IMPRINT",EDGE,{"derivedFrom":subQ5}),1.0]])]});}
            var Q1;
            {var subQ0=sQuery(id+"F15.wireOp",EDGE,"E19.top");var subQ1=sQuery(id+"F15.wireOp",EDGE,"FoTjqakA-3Q0D-e8Zx-aRf2-kQgUUboiUMlV");var subQ2=makeQuery(id+"F15.imprint","INTERSECT",VERTEX,{"derivedFrom":[subQ1,subQ0]});Q1=makeQuery(id+"F15.imprint","IMPRINT",FACE,{"disambiguationData":[TD([[makeQuery(id+"F15.imprint","IMPRINT",EDGE,{"disambiguationData":[TD([[subQ2,1.0]])],"derivedFrom":subQ1}),-1.0]])]});}
            var Q2;
            {var subQ5=sQuery(id+"F15.wireOp",EDGE,"E19.left");Q2=makeQuery(id+"F15.imprint","IMPRINT",FACE,{"disambiguationData":[TD([[makeQuery(id+"F15.imprint","IMPRINT",EDGE,{"derivedFrom":subQ5}),-1.0]])]});}
            var Q3;
            {var subQ0=sQuery(id+"F15.wireOp",EDGE,"1H3nl5ng-9DyI-yJWU-6AWz-InJrUK3OAsY4");Q3=makeQuery(id+"F15.imprint","IMPRINT",FACE,{"disambiguationData":[TD([[makeQuery(id+"F15.imprint","IMPRINT",EDGE,{"derivedFrom":subQ0}),-1.0]])]});}
            var Q4;
            Q4=makeQuery(id+"F15.imprint","IMPRINT",FACE,{"disambiguationData":[TD([[makeQuery(id+"F15.imprint","IMPRINT",EDGE,{"derivedFrom":sQuery(id+"F15.wireOp",EDGE,"tPRg0zax-F67y-5KnP-cIeF-lg8p1GO7OnOK")}),-1.0]])]});
            var Q5;
            Q5=makeQuery(id+"F15.imprint","IMPRINT",FACE,{"disambiguationData":[TD([[makeQuery(id+"F15.imprint","IMPRINT",EDGE,{"derivedFrom":sQuery(id+"F15.wireOp",EDGE,"E39.sketch_text.stroke-0")}),-1.0]])]});
            var Q6;
            Q6=makeQuery(id+"F15.imprint","IMPRINT",FACE,{"disambiguationData":[TD([[makeQuery(id+"F15.imprint","IMPRINT",EDGE,{"derivedFrom":sQuery(id+"F15.wireOp",EDGE,"E39.sketch_text.stroke-13")}),-1.0]])]});
            var Q7;
            Q7=makeQuery(id+"F15.imprint","IMPRINT",FACE,{"disambiguationData":[TD([[makeQuery(id+"F15.imprint","IMPRINT",EDGE,{"derivedFrom":sQuery(id+"F15.wireOp",EDGE,"E38.sketch_text.stroke-18")}),-1.0]])]});
            var Q8;
            Q8=makeQuery(id+"F15.imprint","IMPRINT",FACE,{"disambiguationData":[TD([[makeQuery(id+"F15.imprint","IMPRINT",EDGE,{"derivedFrom":sQuery(id+"F15.wireOp",EDGE,"E38.sketch_text.stroke-0")}),-1.0]])]});
            var Q9;
            Q9=makeQuery(id+"F15.imprint","IMPRINT",FACE,{"disambiguationData":[TD([[makeQuery(id+"F15.imprint","IMPRINT",EDGE,{"derivedFrom":sQuery(id+"F15.wireOp",EDGE,"E38.sketch_text.stroke-19")}),-1.0]])]});
            var Q10;
            Q10=makeQuery(id+"F15.imprint","IMPRINT",FACE,{"disambiguationData":[TD([[makeQuery(id+"F15.imprint","IMPRINT",EDGE,{"derivedFrom":sQuery(id+"F15.wireOp",EDGE,"E46.bottom")}),-1.0]])]});
            var Q11;
            Q11=makeQuery(id+"F15.imprint","IMPRINT",FACE,{"disambiguationData":[TD([[makeQuery(id+"F15.imprint","IMPRINT",EDGE,{"derivedFrom":sQuery(id+"F15.wireOp",EDGE,"E41.bottom")}),1.0]])]});
            var Q12;
            Q12=makeQuery(id+"F15.imprint","IMPRINT",FACE,{"disambiguationData":[TD([[makeQuery(id+"F15.imprint","IMPRINT",EDGE,{"derivedFrom":sQuery(id+"F15.wireOp",EDGE,"E23")}),1.0]])]});
            var Q13;
            Q13=makeQuery(id+"F15.imprint","IMPRINT",FACE,{"disambiguationData":[TD([[makeQuery(id+"F15.imprint","IMPRINT",EDGE,{"derivedFrom":sQuery(id+"F15.wireOp",EDGE,"E20")}),1.0]])]});
            var Q14;
            Q14=makeQuery(id+"F15.imprint","IMPRINT",FACE,{"disambiguationData":[TD([[makeQuery(id+"F15.imprint","IMPRINT",EDGE,{"derivedFrom":sQuery(id+"F15.wireOp",EDGE,"E26")}),1.0]])]});
            extrude(context, id + "F16", {"entities" : qUnion([Q0, Q1, Q2, Q3, Q4, Q5, Q6, Q7, Q8, Q9, Q10, Q11, Q12, Q13, Q14]), "operationType" : NewBodyOperationType.REMOVE, "oppositeDirection" : true, "depth" : 0.2 * mm});
        }
        {
            var Q0;
            Q0=makeQuery(id+"F2.opExtrude","CAP_EDGE",EDGE,{"disambiguationData":[OSD([sQuery(id+"F0.wireOp",EDGE,"E1.right")])],"isStart":false});
            var Q1;
            Q1=makeQuery(id+"F2.opExtrude","SWEPT_EDGE",EDGE,{"disambiguationData":[OSD([sQuery(id+"F0.wireOp",EDGE,"E1.top"),sQuery(id+"F0.wireOp",EDGE,"E1.right")])]});
            var Q2;
            Q2=makeQuery(id+"F2.opExtrude","SWEPT_EDGE",EDGE,{"disambiguationData":[OSD([sQuery(id+"F0.wireOp",EDGE,"E1.bottom"),sQuery(id+"F0.wireOp",EDGE,"E1.right")])]});
            fillet(context, id + "F17", {"entities" : qUnion([Q0, Q1, Q2]), "radius" : 2 * mm, "tangentPropagation" : true, "allowEdgeOverflow" : false});
        }
        {
            var Q0;
            Q0=makeQuery(id+"F2.opExtrude","CAP_EDGE",EDGE,{"disambiguationData":[OSD([sQuery(id+"F0.wireOp",EDGE,"E1.top"),sQuery(id+"F0.wireOp",EDGE,"E11.bottom")])],"isStart":false});
            var Q1;
            Q1=makeQuery(id+"F2.opExtrude","CAP_EDGE",EDGE,{"disambiguationData":[OSD([sQuery(id+"F0.wireOp",EDGE,"E1.bottom"),sQuery(id+"F0.wireOp",EDGE,"E11.top")])],"isStart":false});
            chamfer(context, id + "F18", {"entities" : qUnion([Q0, Q1]), "width" : 2 * mm, "tangentPropagation" : true});
        }
        {
            var Q0;
            Q0=makeQuery(id+"F0.imprint","IMPRINT",FACE,{"disambiguationData":[TD([[makeQuery(id+"F0.imprint","IMPRINT",EDGE,{"derivedFrom":sQuery(id+"F0.wireOp",EDGE,"E7.bottom")}),-1.0]])]});
            var Q1;
            Q1=makeQuery(id+"F0.imprint","IMPRINT",FACE,{"disambiguationData":[TD([[makeQuery(id+"F0.imprint","IMPRINT",EDGE,{"derivedFrom":sQuery(id+"F0.wireOp",EDGE,"E7.bottom")}),1.0]])]});
            var Q2;
            Q2=makeQuery(id+"F0.imprint","IMPRINT",FACE,{"disambiguationData":[TD([[makeQuery(id+"F0.imprint","IMPRINT",EDGE,{"derivedFrom":sQuery(id+"F0.wireOp",EDGE,"E8.bottom")}),1.0]])]});
            var Q3;
            Q3=makeQuery(id+"F0.imprint","IMPRINT",FACE,{"disambiguationData":[TD([[makeQuery(id+"F0.imprint","IMPRINT",EDGE,{"derivedFrom":sQuery(id+"F0.wireOp",EDGE,"E8.bottom")}),-1.0]])]});
            extrude(context, id + "F19", {"entities" : qUnion([Q0, Q1, Q2, Q3]), "operationType" : NewBodyOperationType.REMOVE, "endBound" : BoundingType.THROUGH_ALL, "depth" : 25 * mm});
        }
        {
            var Q0;
            Q0=makeQuery(id+"F0.imprint","IMPRINT",FACE,{"disambiguationData":[TD([[makeQuery(id+"F0.imprint","IMPRINT",EDGE,{"derivedFrom":sQuery(id+"F0.wireOp",EDGE,"E7.bottom")}),1.0]])]});
            var Q1;
            Q1=makeQuery(id+"F0.imprint","IMPRINT",FACE,{"disambiguationData":[TD([[makeQuery(id+"F0.imprint","IMPRINT",EDGE,{"derivedFrom":sQuery(id+"F0.wireOp",EDGE,"E7.bottom")}),-1.0]])]});
            var Q2;
            Q2=makeQuery(id+"F0.imprint","IMPRINT",FACE,{"disambiguationData":[TD([[makeQuery(id+"F0.imprint","IMPRINT",EDGE,{"derivedFrom":sQuery(id+"F0.wireOp",EDGE,"E8.bottom")}),1.0]])]});
            var Q3;
            Q3=makeQuery(id+"F0.imprint","IMPRINT",FACE,{"disambiguationData":[TD([[makeQuery(id+"F0.imprint","IMPRINT",EDGE,{"derivedFrom":sQuery(id+"F0.wireOp",EDGE,"E8.bottom")}),-1.0]])]});
            extrude(context, id + "F20", {"entities" : qUnion([Q0, Q1, Q2, Q3]), "operationType" : NewBodyOperationType.ADD, "depth" : 6.2 * mm});
        }
        {
            var Q0;
            Q0=makeQuery(id+"F0.imprint","IMPRINT",FACE,{"disambiguationData":[TD([[makeQuery(id+"F0.imprint","IMPRINT",EDGE,{"derivedFrom":sQuery(id+"F0.wireOp",EDGE,"E7.bottom")}),1.0]])]});
            var Q1;
            Q1=makeQuery(id+"F0.imprint","IMPRINT",FACE,{"disambiguationData":[TD([[makeQuery(id+"F0.imprint","IMPRINT",EDGE,{"derivedFrom":sQuery(id+"F0.wireOp",EDGE,"E8.bottom")}),1.0]])]});
            var Q2;
            Q2=makeQuery(id+"F0.imprint","IMPRINT",FACE,{"disambiguationData":[TD([[makeQuery(id+"F0.imprint","IMPRINT",EDGE,{"derivedFrom":sQuery(id+"F0.wireOp",EDGE,"E7.bottom")}),-1.0]])]});
            var Q3;
            Q3=makeQuery(id+"F0.imprint","IMPRINT",FACE,{"disambiguationData":[TD([[makeQuery(id+"F0.imprint","IMPRINT",EDGE,{"derivedFrom":sQuery(id+"F0.wireOp",EDGE,"E8.bottom")}),-1.0]])]});
            extrude(context, id + "F21", {"entities" : qUnion([Q0, Q1, Q2, Q3]), "operationType" : NewBodyOperationType.REMOVE, "depth" : 5.7 * mm});
        }
        {
            var Q0;
            Q0=makeQuery(id+"F1.opExtrude","SWEPT_FACE",FACE,{"disambiguationData":[OSD([sQuery(id+"F0.wireOp",EDGE,"E0.top"),sQuery(id+"F0.wireOp",EDGE,"E9.bottom"),sQuery(id+"F0.wireOp",EDGE,"E10.bottom")])]});
            var sketch = newSketch(context, id + "F22", { "sketchPlane" : qUnion([Q0])});
            skText(sketch, "E61", { "text": "5V", "fontName": "OpenSans-Bold.ttf"});
            skLineSegment(sketch, "E62.bottom", {"start": v(-9.26, 2.92) * mm, "end": v(-7.89, 2.92) * mm});
            skLineSegment(sketch, "E62.top", {"start": v(-9.26, 0.45) * mm, "end": v(-7.89, 0.45) * mm});
            skLineSegment(sketch, "E62.left", {"start": v(-9.46, 2.72) * mm, "end": v(-9.46, 0.65) * mm});
            skLineSegment(sketch, "E62.right", {"start": v(-7.69, 2.72) * mm, "end": v(-7.69, 0.65) * mm});
            skLineSegment(sketch, "E63.bottom", {"start": v(-8.88, 3.22) * mm, "end": v(-8.25, 3.22) * mm});
            skLineSegment(sketch, "E63.top", {"start": v(-9.08, 3.23) * mm, "end": v(-8.05, 3.23) * mm});
            skLineSegment(sketch, "E63.left", {"start": v(-9.08, 3.02) * mm, "end": v(-9.08, 2.92) * mm});
            skLineSegment(sketch, "E63.right", {"start": v(-8.05, 3.02) * mm, "end": v(-8.05, 2.92) * mm});
            skPoint(sketch, "E64.visualSharp", {"position": v(-9.46, 3.23) * mm});
            skArc(sketch, "E64.filletArc", {"start": v(-9.26, 2.92) * mm, "mid": v(-9.4, 2.86) * mm, "end": v(-9.46, 2.72) * mm});
            skPoint(sketch, "E65.visualSharp", {"position": v(-7.69, 3.23) * mm});
            skArc(sketch, "E65.filletArc", {"start": v(-7.69, 2.72) * mm, "mid": v(-7.75, 2.86) * mm, "end": v(-7.89, 2.92) * mm});
            skPoint(sketch, "E66.visualSharp", {"position": v(-9.46, 0.76) * mm});
            skArc(sketch, "E66.filletArc", {"start": v(-9.46, 0.65) * mm, "mid": v(-9.4, 0.5) * mm, "end": v(-9.26, 0.45) * mm});
            skPoint(sketch, "E67.visualSharp", {"position": v(-7.69, 0.76) * mm});
            skArc(sketch, "E67.filletArc", {"start": v(-7.89, 0.45) * mm, "mid": v(-7.75, 0.5) * mm, "end": v(-7.69, 0.65) * mm});
            skPoint(sketch, "E68.visualSharp", {"position": v(-9.08, 3.53) * mm});
            skArc(sketch, "E68.filletArc", {"start": v(-8.88, 3.22) * mm, "mid": v(-9.02, 3.16) * mm, "end": v(-9.08, 3.02) * mm});
            skPoint(sketch, "E69.visualSharp", {"position": v(-8.05, 3.53) * mm});
            skArc(sketch, "E69.filletArc", {"start": v(-8.05, 3.02) * mm, "mid": v(-8.1, 3.16) * mm, "end": v(-8.25, 3.22) * mm});
            skLineSegment(sketch, "E70.bottom", {"start": v(-9.11, 1.09) * mm, "end": v(-8, 1.09) * mm});
            skLineSegment(sketch, "E70.top", {"start": v(-9.11, 0.76) * mm, "end": v(-8, 0.76) * mm});
            skLineSegment(sketch, "E70.left", {"start": v(-9.11, 1.09) * mm, "end": v(-9.11, 0.76) * mm});
            skLineSegment(sketch, "E70.right", {"start": v(-8, 1.09) * mm, "end": v(-8, 0.76) * mm});
            skLineSegment(sketch, "E71.MirrorCS", {"start": v(-9.11, 1.41) * mm, "end": v(-8, 1.41) * mm});
            skLineSegment(sketch, "E72.bottom", {"start": v(-9.11, 1.74) * mm, "end": v(-8, 1.74) * mm});
            skLineSegment(sketch, "E72.top", {"start": v(-9.11, 1.73) * mm, "end": v(-8, 1.73) * mm});
            skLineSegment(sketch, "E72.left", {"start": v(-9.11, 1.74) * mm, "end": v(-9.11, 1.41) * mm});
            skLineSegment(sketch, "E72.right", {"start": v(-8, 1.74) * mm, "end": v(-8, 1.41) * mm});
            skLineSegment(sketch, "E73.MirrorCS", {"start": v(-9.11, 2.38) * mm, "end": v(-8, 2.38) * mm});
            skLineSegment(sketch, "E74.MirrorCS", {"start": v(-9.11, 2.06) * mm, "end": v(-8, 2.06) * mm});
            skLineSegment(sketch, "E75.bottom", {"start": v(-9.11, 2.4) * mm, "end": v(-8, 2.4) * mm});
            skLineSegment(sketch, "E75.left", {"start": v(-9.11, 2.4) * mm, "end": v(-9.11, 2.06) * mm});
            skLineSegment(sketch, "E75.right", {"start": v(-8, 2.4) * mm, "end": v(-8, 2.06) * mm});
            skLineSegment(sketch, "E76", {"start": v(-17.4, 3.32) * mm, "end": v(-16.81, 3.32) * mm});
            skLineSegment(sketch, "E77", {"start": v(-17.35, 2.16) * mm, "end": v(-16.59, 2.18) * mm});
            skLineSegment(sketch, "E78", {"start": v(-16.59, 2.18) * mm, "end": v(-18.15, 0.47) * mm});
            skLineSegment(sketch, "E79", {"start": v(-18.15, 0.47) * mm, "end": v(-17.5, 1.75) * mm});
            skLineSegment(sketch, "E80", {"start": v(-17.5, 1.75) * mm, "end": v(-18.15, 1.74) * mm});
            skLineSegment(sketch, "E81", {"start": v(-18.15, 1.74) * mm, "end": v(-17.4, 3.32) * mm});
            skLineSegment(sketch, "E82", {"start": v(-16.81, 3.32) * mm, "end": v(-17.35, 2.16) * mm});
            const initialGuessF22  = {"E61": [-0.03421, 0.0006, 1, 0, 0.0025]};
            skSetInitialGuess(sketch, initialGuessF22);
            skSolve(sketch);
        }
        {
            var Q0;
            Q0 = qSketchRegion(id + "F22", true);
            extrude(context, id + "F23", {"entities" : qUnion([Q0]), "operationType" : NewBodyOperationType.REMOVE, "oppositeDirection" : true, "depth" : 0.2 * mm});
        }
        {
            var Q0;
            Q0=makeQuery(id+"F15.imprint","IMPRINT",FACE,{"disambiguationData":[TD([[makeQuery(id+"F15.imprint","IMPRINT",EDGE,{"derivedFrom":sQuery(id+"F15.wireOp",EDGE,"E40.sketch_text.stroke-29")}),-1.0]])]});
            var Q1;
            Q1=makeQuery(id+"F15.imprint","IMPRINT",FACE,{"disambiguationData":[TD([[makeQuery(id+"F15.imprint","IMPRINT",EDGE,{"derivedFrom":sQuery(id+"F15.wireOp",EDGE,"E40.sketch_text.stroke-48")}),-1.0]])]});
            var Q2;
            Q2=makeQuery(id+"F15.imprint","IMPRINT",FACE,{"disambiguationData":[TD([[makeQuery(id+"F15.imprint","IMPRINT",EDGE,{"derivedFrom":sQuery(id+"F15.wireOp",EDGE,"E40.sketch_text.stroke-15")}),-1.0]])]});
            var Q3;
            Q3=makeQuery(id+"F15.imprint","IMPRINT",FACE,{"disambiguationData":[TD([[makeQuery(id+"F15.imprint","IMPRINT",EDGE,{"derivedFrom":sQuery(id+"F15.wireOp",EDGE,"E40.sketch_text.stroke-0")}),-1.0]])]});
            extrude(context, id + "F24", {"entities" : qUnion([Q0, Q1, Q2, Q3]), "operationType" : NewBodyOperationType.REMOVE, "oppositeDirection" : true, "depth" : 0.2 * mm});
        }
        {
            var Q0;
            Q0=makeQuery(id+"F7.boolean.opBoolean","COPY",FACE,{"derivedFrom":makeQuery(id+"F7.opExtrude","CAP_FACE",FACE,{"disambiguationData":[OSD([sQuery(id+"F0.wireOp",EDGE,"E5.top"),sQuery(id+"F0.wireOp",EDGE,"E5.left"),sQuery(id+"F0.wireOp",EDGE,"E5.right"),sQuery(id+"F0.wireOp",EDGE,"E9.bottom"),sQuery(id+"F0.wireOp",EDGE,"E9.top"),sQuery(id+"F0.wireOp",EDGE,"E9.left"),sQuery(id+"F0.wireOp",EDGE,"E9.right")])],"isStart":false})});
            extrude(context, id + "F25", {"entities" : qUnion([Q0]), "operationType" : NewBodyOperationType.ADD, "depth" : 0.3 * mm});
        }
        {
            var Q0;
            Q0=makeQuery(id+"F25.opExtrude","CAP_FACE",FACE,{"disambiguationData":[OSD([sQuery(id+"F0.wireOp",EDGE,"E5.top"),sQuery(id+"F0.wireOp",EDGE,"E5.left"),sQuery(id+"F0.wireOp",EDGE,"E5.right"),sQuery(id+"F0.wireOp",EDGE,"E9.bottom"),sQuery(id+"F0.wireOp",EDGE,"E9.top"),sQuery(id+"F0.wireOp",EDGE,"E9.left"),sQuery(id+"F0.wireOp",EDGE,"E9.right")])],"isStart":false});
            var sketch = newSketch(context, id + "F26", { "sketchPlane" : qUnion([Q0])});
            skLineSegment(sketch, "E83.bottom", {"start": v(-29.5, 16.5) * mm, "end": v(-25.5, 16.5) * mm});
            skLineSegment(sketch, "E83.top", {"start": v(-29.5, 14.5) * mm, "end": v(-25.5, 14.5) * mm});
            skLineSegment(sketch, "E83.left", {"start": v(-29.5, 16.5) * mm, "end": v(-29.5, 14.5) * mm});
            skLineSegment(sketch, "E83.right", {"start": v(-25.5, 16.5) * mm, "end": v(-25.5, 14.5) * mm});
            skSolve(sketch);
        }
        {
            var Q0;
            Q0=makeQuery(id+"F26.imprint","IMPRINT",FACE,{"disambiguationData":[TD([[makeQuery(id+"F26.imprint","IMPRINT",EDGE,{"derivedFrom":sQuery(id+"F26.wireOp",EDGE,"E83.bottom")}),1.0]])]});
            extrude(context, id + "F27", {"entities" : qUnion([Q0]), "operationType" : NewBodyOperationType.ADD, "depth" : 3.7 * mm});
        }
        {
            var Q0;
            Q0=makeQuery(id+"F26.imprint","IMPRINT",FACE,{"disambiguationData":[TD([[makeQuery(id+"F26.imprint","IMPRINT",EDGE,{"derivedFrom":sQuery(id+"F26.wireOp",EDGE,"E83.bottom")}),1.0]])]});
            extrude(context, id + "F28", {"entities" : qUnion([Q0]), "operationType" : NewBodyOperationType.REMOVE, "depth" : 3.4 * mm});
        }
        {
            var Q0;
            Q0=makeQuery(id+"F7.boolean.opBoolean","COPY",FACE,{"derivedFrom":makeQuery(id+"F7.opExtrude","CAP_FACE",FACE,{"disambiguationData":[OSD([sQuery(id+"F0.wireOp",EDGE,"E0.top"),sQuery(id+"F0.wireOp",EDGE,"E6.top"),sQuery(id+"F0.wireOp",EDGE,"E6.left"),sQuery(id+"F0.wireOp",EDGE,"E6.right"),sQuery(id+"F0.wireOp",EDGE,"E10.bottom"),sQuery(id+"F0.wireOp",EDGE,"E10.top"),sQuery(id+"F0.wireOp",EDGE,"E10.left"),sQuery(id+"F0.wireOp",EDGE,"E10.right")])],"isStart":false})});
            extrude(context, id + "F29", {"entities" : qUnion([Q0]), "operationType" : NewBodyOperationType.ADD, "depth" : 0.3 * mm});
        }
        {
            var Q0;
            Q0=makeQuery(id+"F29.opExtrude","CAP_FACE",FACE,{"disambiguationData":[OSD([sQuery(id+"F0.wireOp",EDGE,"E0.top"),sQuery(id+"F0.wireOp",EDGE,"E6.top"),sQuery(id+"F0.wireOp",EDGE,"E6.left"),sQuery(id+"F0.wireOp",EDGE,"E6.right"),sQuery(id+"F0.wireOp",EDGE,"E10.bottom"),sQuery(id+"F0.wireOp",EDGE,"E10.top"),sQuery(id+"F0.wireOp",EDGE,"E10.left"),sQuery(id+"F0.wireOp",EDGE,"E10.right")])],"isStart":false});
            var sketch = newSketch(context, id + "F30", { "sketchPlane" : qUnion([Q0])});
            skLineSegment(sketch, "E84.bottom", {"start": v(-15.5, 14.5) * mm, "end": v(-10, 14.5) * mm});
            skLineSegment(sketch, "E84.top", {"start": v(-15.5, 16.5) * mm, "end": v(-10, 16.5) * mm});
            skLineSegment(sketch, "E84.left", {"start": v(-15.5, 14.5) * mm, "end": v(-15.5, 16.5) * mm});
            skLineSegment(sketch, "E84.right", {"start": v(-10, 14.5) * mm, "end": v(-10, 16.5) * mm});
            skSolve(sketch);
        }
        {
            var Q0;
            Q0=makeQuery(id+"F30.imprint","IMPRINT",FACE,{"disambiguationData":[TD([[makeQuery(id+"F30.imprint","IMPRINT",EDGE,{"derivedFrom":sQuery(id+"F30.wireOp",EDGE,"E84.bottom")}),-1.0]])]});
            extrude(context, id + "F31", {"entities" : qUnion([Q0]), "operationType" : NewBodyOperationType.ADD, "depth" : 3.7 * mm});
        }
        {
            var Q0;
            Q0=makeQuery(id+"F30.imprint","IMPRINT",FACE,{"disambiguationData":[TD([[makeQuery(id+"F30.imprint","IMPRINT",EDGE,{"derivedFrom":sQuery(id+"F30.wireOp",EDGE,"E84.bottom")}),-1.0]])]});
            extrude(context, id + "F32", {"entities" : qUnion([Q0]), "operationType" : NewBodyOperationType.REMOVE, "depth" : 3.4 * mm});
        }
        {
            var Q0;
            {var subQ1=sQuery(id+"F0.wireOp",EDGE,"E1.bottom");var subQ3=sQuery(id+"F0.wireOp",EDGE,"E11.bottom");var subQ4=sQuery(id+"F0.wireOp",EDGE,"E1.top");var subQ5=sQuery(id+"F0.wireOp",EDGE,"E1.right");var subQ6=makeQuery(id+"F2.opExtrude","SWEPT_FACE",FACE,{"disambiguationData":[OSD([subQ5])]});var subQ8=sQuery(id+"F0.wireOp",EDGE,"E11.top");var subQ14=sQuery(id+"F0.wireOp",EDGE,"E3");var subQ15=sQuery(id+"F0.wireOp",EDGE,"E1.left");var subQ16=sQuery(id+"F0.wireOp",EDGE,"E4");var subQ17=sQuery(id+"F0.wireOp",EDGE,"E2");Q0=makeQuery(id+"F14.boolean.opBoolean","SPLIT",FACE,{"disambiguationData":[TD([subQ6])],"derivedFrom":makeQuery(id+"F11.boolean.opBoolean","SPLIT",FACE,{"disambiguationData":[TD([subQ6])],"derivedFrom":makeQuery(id+"F9.boolean.opBoolean","MERGE",FACE,{"derivedFrom":[makeQuery(id+"F5.opShell","OFFSET_FACE",FACE,{"disambiguationData":[OSD([sQuery(id+"F0.wireOp",EDGE,"E0.bottom"),sQuery(id+"F0.wireOp",EDGE,"E0.top"),sQuery(id+"F0.wireOp",EDGE,"E0.right"),subQ1,subQ4,subQ15,subQ5,subQ17,subQ14,subQ16,sQuery(id+"F0.wireOp",EDGE,"E9.bottom"),sQuery(id+"F0.wireOp",EDGE,"E9.top"),sQuery(id+"F0.wireOp",EDGE,"E9.left"),sQuery(id+"F0.wireOp",EDGE,"E9.right"),sQuery(id+"F0.wireOp",EDGE,"E10.bottom"),sQuery(id+"F0.wireOp",EDGE,"E10.top"),sQuery(id+"F0.wireOp",EDGE,"E10.left"),sQuery(id+"F0.wireOp",EDGE,"E10.right"),subQ3,subQ8,sQuery(id+"F0.wireOp",EDGE,"E17.0"),sQuery(id+"F0.wireOp",EDGE,"E17.1"),sQuery(id+"F0.wireOp",EDGE,"E17.2"),sQuery(id+"F0.wireOp",EDGE,"E17.3"),sQuery(id+"F0.wireOp",EDGE,"E18.0"),sQuery(id+"F0.wireOp",EDGE,"E18.1"),sQuery(id+"F0.wireOp",EDGE,"E18.2"),sQuery(id+"F0.wireOp",EDGE,"E18.3")])]}),makeQuery(id+"F9.opExtrude","SWEPT_FACE",FACE,{"disambiguationData":[OSD([subQ5]),TDD([makeQuery(id+"F5.opShell","OFFSET_EDGE",EDGE,{"disambiguationData":[OSD([subQ5]),TDD([makeQuery(id+"F2.opExtrude","CAP_EDGE",EDGE,{"disambiguationData":[OSD([subQ5])],"isStart":false})])]})])]})]})})});}
            var Q1;
            {var subQ1=sQuery(id+"F0.wireOp",EDGE,"E1.top");var subQ3=sQuery(id+"F0.wireOp",EDGE,"E11.top");var subQ4=sQuery(id+"F0.wireOp",EDGE,"E1.bottom");var subQ7=sQuery(id+"F0.wireOp",EDGE,"E14");var subQ8=sQuery(id+"F0.wireOp",EDGE,"E11.bottom");var subQ10=sQuery(id+"F0.wireOp",EDGE,"E1.right");var subQ13=sQuery(id+"F0.wireOp",EDGE,"E3");var subQ14=sQuery(id+"F0.wireOp",EDGE,"E1.left");var subQ15=sQuery(id+"F0.wireOp",EDGE,"E4");var subQ16=sQuery(id+"F0.wireOp",EDGE,"E2");Q1=makeQuery(id+"F14.boolean.opBoolean","SPLIT",FACE,{"disambiguationData":[TD([makeQuery(id+"F14.opExtrude","SWEPT_FACE",FACE,{"disambiguationData":[OSD([subQ7])]})])],"derivedFrom":makeQuery(id+"F11.boolean.opBoolean","SPLIT",FACE,{"disambiguationData":[TD([makeQuery(id+"F2.opExtrude","SWEPT_FACE",FACE,{"disambiguationData":[OSD([subQ10])]})])],"derivedFrom":makeQuery(id+"F9.boolean.opBoolean","MERGE",FACE,{"derivedFrom":[makeQuery(id+"F5.opShell","OFFSET_FACE",FACE,{"disambiguationData":[OSD([sQuery(id+"F0.wireOp",EDGE,"E0.bottom"),sQuery(id+"F0.wireOp",EDGE,"E0.top"),sQuery(id+"F0.wireOp",EDGE,"E0.right"),subQ4,subQ1,subQ14,subQ10,subQ16,subQ13,subQ15,sQuery(id+"F0.wireOp",EDGE,"E9.bottom"),sQuery(id+"F0.wireOp",EDGE,"E9.top"),sQuery(id+"F0.wireOp",EDGE,"E9.left"),sQuery(id+"F0.wireOp",EDGE,"E9.right"),sQuery(id+"F0.wireOp",EDGE,"E10.bottom"),sQuery(id+"F0.wireOp",EDGE,"E10.top"),sQuery(id+"F0.wireOp",EDGE,"E10.left"),sQuery(id+"F0.wireOp",EDGE,"E10.right"),subQ8,subQ3,sQuery(id+"F0.wireOp",EDGE,"E17.0"),sQuery(id+"F0.wireOp",EDGE,"E17.1"),sQuery(id+"F0.wireOp",EDGE,"E17.2"),sQuery(id+"F0.wireOp",EDGE,"E17.3"),sQuery(id+"F0.wireOp",EDGE,"E18.0"),sQuery(id+"F0.wireOp",EDGE,"E18.1"),sQuery(id+"F0.wireOp",EDGE,"E18.2"),sQuery(id+"F0.wireOp",EDGE,"E18.3")])]}),makeQuery(id+"F9.opExtrude","SWEPT_FACE",FACE,{"disambiguationData":[OSD([subQ10]),TDD([makeQuery(id+"F5.opShell","OFFSET_EDGE",EDGE,{"disambiguationData":[OSD([subQ10]),TDD([makeQuery(id+"F2.opExtrude","CAP_EDGE",EDGE,{"disambiguationData":[OSD([subQ10])],"isStart":false})])]})])]})]})})});}
            extrude(context, id + "F33", {"entities" : qUnion([Q0, Q1]), "operationType" : NewBodyOperationType.ADD, "depth" : 0.5 * mm});
        }
        {
            var Q0;
            Q0=makeQuery(id+"F14.boolean.opBoolean","COPY",FACE,{"derivedFrom":makeQuery(id+"F14.opExtrude","CAP_FACE",FACE,{"disambiguationData":[OSD([sQuery(id+"F0.wireOp",EDGE,"E1.bottom"),sQuery(id+"F0.wireOp",EDGE,"E1.top"),sQuery(id+"F0.wireOp",EDGE,"E15"),sQuery(id+"F0.wireOp",EDGE,"E16")])],"isStart":false})});
            extrude(context, id + "F34", {"entities" : qUnion([Q0]), "operationType" : NewBodyOperationType.REMOVE, "oppositeDirection" : true, "depth" : 0.3 * mm});
        }
        {
            var Q0;
            {var subQ0=sQuery(id+"F0.wireOp",EDGE,"E3");var subQ1=sQuery(id+"F0.wireOp",EDGE,"E2");var subQ2=sQuery(id+"F0.wireOp",EDGE,"E0.right");var subQ3=sQuery(id+"F0.wireOp",EDGE,"E0.bottom");var subQ4=sQuery(id+"F0.wireOp",EDGE,"E10.bottom");var subQ5=sQuery(id+"F0.wireOp",EDGE,"E9.bottom");var subQ6=sQuery(id+"F0.wireOp",EDGE,"E0.top");var subQ7=sQuery(id+"F0.wireOp",EDGE,"E1.right");Q0=makeQuery(id+"F11.boolean.opBoolean","SPLIT",FACE,{"disambiguationData":[TD([makeQuery(id+"F5.opShell","OFFSET_FACE",FACE,{"disambiguationData":[OSD([subQ3])]})])],"derivedFrom":makeQuery(id+"F9.boolean.opBoolean","MERGE",FACE,{"derivedFrom":[makeQuery(id+"F5.opShell","OFFSET_FACE",FACE,{"disambiguationData":[OSD([subQ3,subQ6,subQ2,sQuery(id+"F0.wireOp",EDGE,"E1.bottom"),sQuery(id+"F0.wireOp",EDGE,"E1.top"),sQuery(id+"F0.wireOp",EDGE,"E1.left"),subQ7,subQ1,subQ0,sQuery(id+"F0.wireOp",EDGE,"E4"),subQ5,sQuery(id+"F0.wireOp",EDGE,"E9.top"),sQuery(id+"F0.wireOp",EDGE,"E9.left"),sQuery(id+"F0.wireOp",EDGE,"E9.right"),subQ4,sQuery(id+"F0.wireOp",EDGE,"E10.top"),sQuery(id+"F0.wireOp",EDGE,"E10.left"),sQuery(id+"F0.wireOp",EDGE,"E10.right"),sQuery(id+"F0.wireOp",EDGE,"E11.bottom"),sQuery(id+"F0.wireOp",EDGE,"E11.top"),sQuery(id+"F0.wireOp",EDGE,"E17.0"),sQuery(id+"F0.wireOp",EDGE,"E17.1"),sQuery(id+"F0.wireOp",EDGE,"E17.2"),sQuery(id+"F0.wireOp",EDGE,"E17.3"),sQuery(id+"F0.wireOp",EDGE,"E18.0"),sQuery(id+"F0.wireOp",EDGE,"E18.1"),sQuery(id+"F0.wireOp",EDGE,"E18.2"),sQuery(id+"F0.wireOp",EDGE,"E18.3")])]}),makeQuery(id+"F9.opExtrude","SWEPT_FACE",FACE,{"disambiguationData":[OSD([subQ7]),TDD([makeQuery(id+"F5.opShell","OFFSET_EDGE",EDGE,{"disambiguationData":[OSD([subQ7]),TDD([makeQuery(id+"F2.opExtrude","CAP_EDGE",EDGE,{"disambiguationData":[OSD([subQ7])],"isStart":false})])]})])]})]})});}
            var sketch = newSketch(context, id + "F35", { "sketchPlane" : qUnion([Q0])});
            skLineSegment(sketch, "E85.bottom", {"start": v(-30.25, 14.5) * mm, "end": v(0, 14.5) * mm});
            skLineSegment(sketch, "E85.top", {"start": v(-30.25, 2.33) * mm, "end": v(0, 2.33) * mm});
            skLineSegment(sketch, "E85.left", {"start": v(-30.25, 14.5) * mm, "end": v(-30.25, 2.33) * mm});
            skLineSegment(sketch, "E85.right", {"start": v(0, 14.5) * mm, "end": v(0, 2.33) * mm});
            skLineSegment(sketch, "E86.bottom", {"start": v(-18.2, 7.5) * mm, "end": v(-22.2, 7.5) * mm});
            skLineSegment(sketch, "E86.top", {"start": v(-18.2, 13) * mm, "end": v(-22.2, 13) * mm});
            skLineSegment(sketch, "E86.left", {"start": v(-18.2, 7.5) * mm, "end": v(-18.2, 13) * mm});
            skLineSegment(sketch, "E86.right", {"start": v(-22.2, 7.5) * mm, "end": v(-22.2, 13) * mm});
            skPoint(sketch, "E86.middle", {"position": v(-20.2, 10.25) * mm});
            skPoint(sketch, "E86.middle.positionSnap0", {"position": v(-18.7, 10.25) * mm});
            skPoint(sketch, "E86.centerSnap0", {"position": v(-18.7, 10.25) * mm});
            skLineSegment(sketch, "E87.bottom", {"start": v(-5.5, 7.5) * mm, "end": v(-9.5, 7.5) * mm});
            skLineSegment(sketch, "E87.top", {"start": v(-5.5, 13) * mm, "end": v(-9.5, 13) * mm});
            skLineSegment(sketch, "E87.left", {"start": v(-5.5, 7.5) * mm, "end": v(-5.5, 13) * mm});
            skLineSegment(sketch, "E87.right", {"start": v(-9.5, 7.5) * mm, "end": v(-9.5, 13) * mm});
            skPoint(sketch, "E87.middle", {"position": v(-7.5, 10.25) * mm});
            skSolve(sketch);
        }
        {
            var Q0;
            Q0=makeQuery(id+"F35.imprint","IMPRINT",FACE,{"disambiguationData":[TD([[makeQuery(id+"F35.imprint","IMPRINT",EDGE,{"derivedFrom":sQuery(id+"F35.wireOp",EDGE,"E85.bottom")}),1.0]])]});
            extrude(context, id + "F36", {"entities" : qUnion([Q0]), "operationType" : NewBodyOperationType.ADD, "depth" : 0.8 * mm});
        }
        {
            var Q0;
            Q0=makeQuery(id+"F36.opExtrude","CAP_EDGE",EDGE,{"disambiguationData":[OSD([sQuery(id+"F35.wireOp",EDGE,"E85.left")])],"isStart":false});
            var Q1;
            Q1=makeQuery(id+"F36.opExtrude","CAP_EDGE",EDGE,{"disambiguationData":[OSD([sQuery(id+"F35.wireOp",EDGE,"E85.right")])],"isStart":false});
            chamfer(context, id + "F37", {"entities" : qUnion([Q0, Q1]), "width" : 0.8 * mm, "tangentPropagation" : true});
        }
        {
            var Q0;
            Q0=makeQuery(id+"F5.opShell","OFFSET_FACE",FACE,{"disambiguationData":[OSD([sQuery(id+"F0.wireOp",EDGE,"E0.bottom")])]});
            var sketch = newSketch(context, id + "F38", { "sketchPlane" : qUnion([Q0])});
            skLineSegment(sketch, "E88.bottom", {"start": v(-36, 0) * mm, "end": v(-33, 0) * mm});
            skLineSegment(sketch, "E88.top", {"start": v(-36, 2) * mm, "end": v(-33, 2) * mm});
            skLineSegment(sketch, "E88.left", {"start": v(-36, 0) * mm, "end": v(-36, 2) * mm});
            skLineSegment(sketch, "E88.right", {"start": v(-33, 0) * mm, "end": v(-33, 2) * mm});
            skLineSegment(sketch, "E89.1.0.0", {"start": v(-21, 0) * mm, "end": v(-18, 0) * mm});
            skLineSegment(sketch, "E89.1.0.1", {"start": v(-21, 2) * mm, "end": v(-18, 2) * mm});
            skLineSegment(sketch, "E89.1.0.2", {"start": v(-18, 0) * mm, "end": v(-18, 2) * mm});
            skLineSegment(sketch, "E89.1.0.3", {"start": v(-21, 0) * mm, "end": v(-21, 2) * mm});
            skLineSegment(sketch, "E89.2.0.0", {"start": v(-6, 0) * mm, "end": v(-3, 0) * mm});
            skLineSegment(sketch, "E89.2.0.1", {"start": v(-6, 2) * mm, "end": v(-3, 2) * mm});
            skLineSegment(sketch, "E89.2.0.2", {"start": v(-3, 0) * mm, "end": v(-3, 2) * mm});
            skLineSegment(sketch, "E89.2.0.3", {"start": v(-6, 0) * mm, "end": v(-6, 2) * mm});
            skLineSegment(sketch, "E89.direction1", {"start": v(-37, 0) * mm, "end": v(-22, 0) * mm, "construction": true});
            skSolve(sketch);
        }
        {
            var Q0;
            Q0=makeQuery(id+"F38.imprint","IMPRINT",FACE,{"disambiguationData":[TD([[makeQuery(id+"F38.imprint","IMPRINT",EDGE,{"derivedFrom":sQuery(id+"F38.wireOp",EDGE,"E88.bottom")}),-1.0]])]});
            var Q1;
            Q1=makeQuery(id+"F38.imprint","IMPRINT",FACE,{"disambiguationData":[TD([[makeQuery(id+"F38.imprint","IMPRINT",EDGE,{"derivedFrom":sQuery(id+"F38.wireOp",EDGE,"E89.1.0.0")}),-1.0]])]});
            var Q2;
            Q2=makeQuery(id+"F38.imprint","IMPRINT",FACE,{"disambiguationData":[TD([[makeQuery(id+"F38.imprint","IMPRINT",EDGE,{"derivedFrom":sQuery(id+"F38.wireOp",EDGE,"E89.2.0.0")}),-1.0]])]});
            extrude(context, id + "F39", {"entities" : qUnion([Q0, Q1, Q2]), "operationType" : NewBodyOperationType.ADD, "endBound" : BoundingType.UP_TO_NEXT, "depth" : 25 * mm});
        }
        {
            var Q0;
            {var subQ0=sQuery(id+"F0.wireOp",EDGE,"E1.top");var subQ1=sQuery(id+"F0.wireOp",EDGE,"E11.bottom");Q0=makeQuery(id+"F34.boolean.opBoolean","MERGE",FACE,{"derivedFrom":[makeQuery(id+"F14.boolean.opBoolean","MERGE",FACE,{"derivedFrom":[makeQuery(id+"F12.boolean.opBoolean","MERGE",FACE,{"derivedFrom":[makeQuery(id+"F9.boolean.opBoolean","MERGE",FACE,{"derivedFrom":[makeQuery(id+"F5.opShell","OFFSET_FACE",FACE,{"disambiguationData":[OSD([subQ0,subQ1])]}),makeQuery(id+"F9.opExtrude","SWEPT_FACE",FACE,{"disambiguationData":[OSD([subQ0,sQuery(id+"F0.wireOp",EDGE,"E1.right")])]})]}),makeQuery(id+"F12.opExtrude","SWEPT_FACE",FACE,{"disambiguationData":[OSD([subQ0,subQ1])]})]}),makeQuery(id+"F14.opExtrude","SWEPT_FACE",FACE,{"disambiguationData":[OSD([subQ0]),TDD([makeQuery(id+"F0.imprint","IMPRINT",EDGE,{"disambiguationData":[TD([[makeQuery(id+"F0.imprint","INTERSECT",VERTEX,{"derivedFrom":[subQ0,sQuery(id+"F0.wireOp",EDGE,"E14")]}),1.0]])],"derivedFrom":subQ0})])]}),makeQuery(id+"F14.opExtrude","SWEPT_FACE",FACE,{"disambiguationData":[OSD([subQ0]),TDD([makeQuery(id+"F0.imprint","IMPRINT",EDGE,{"disambiguationData":[TD([[makeQuery(id+"F0.imprint","INTERSECT",VERTEX,{"derivedFrom":[subQ0,sQuery(id+"F0.wireOp",EDGE,"E15")]}),1.0]])],"derivedFrom":subQ0})])]})]}),makeQuery(id+"F34.opExtrude","SWEPT_FACE",FACE,{"disambiguationData":[OSD([subQ0])]})]});}
            var sketch = newSketch(context, id + "F40", { "sketchPlane" : qUnion([Q0])});
            skLineSegment(sketch, "E90.bottom", {"start": v(-6, 0) * mm, "end": v(-8, 0) * mm});
            skLineSegment(sketch, "E90.top", {"start": v(-6, 2) * mm, "end": v(-8, 2) * mm});
            skLineSegment(sketch, "E90.left", {"start": v(-6, 0) * mm, "end": v(-6, 2) * mm});
            skLineSegment(sketch, "E90.right", {"start": v(-8, 0) * mm, "end": v(-8, 2) * mm});
            skLineSegment(sketch, "E91.1.0.0", {"start": v(-19, 0) * mm, "end": v(-21, 0) * mm});
            skLineSegment(sketch, "E91.1.0.1", {"start": v(-19, 0) * mm, "end": v(-19, 2) * mm});
            skLineSegment(sketch, "E91.1.0.2", {"start": v(-21, 0) * mm, "end": v(-21, 2) * mm});
            skLineSegment(sketch, "E91.1.0.3", {"start": v(-19, 2) * mm, "end": v(-21, 2) * mm});
            skLineSegment(sketch, "E91.2.0.0", {"start": v(-32, 0) * mm, "end": v(-34, 0) * mm});
            skLineSegment(sketch, "E91.2.0.1", {"start": v(-32, 0) * mm, "end": v(-32, 2) * mm});
            skLineSegment(sketch, "E91.2.0.2", {"start": v(-34, 0) * mm, "end": v(-34, 2) * mm});
            skLineSegment(sketch, "E91.2.0.3", {"start": v(-32, 2) * mm, "end": v(-34, 2) * mm});
            skLineSegment(sketch, "E91.direction1", {"start": v(-8, 0) * mm, "end": v(-21, 0) * mm, "construction": true});
            skSolve(sketch);
        }
        {
            var Q0;
            Q0=makeQuery(id+"F40.imprint","IMPRINT",FACE,{"disambiguationData":[TD([[makeQuery(id+"F40.imprint","IMPRINT",EDGE,{"derivedFrom":sQuery(id+"F40.wireOp",EDGE,"E90.bottom")}),-1.0]])]});
            var Q1;
            Q1=makeQuery(id+"F40.imprint","IMPRINT",FACE,{"disambiguationData":[TD([[makeQuery(id+"F40.imprint","IMPRINT",EDGE,{"derivedFrom":sQuery(id+"F40.wireOp",EDGE,"E91.1.0.0")}),-1.0]])]});
            var Q2;
            Q2=makeQuery(id+"F40.imprint","IMPRINT",FACE,{"disambiguationData":[TD([[makeQuery(id+"F40.imprint","IMPRINT",EDGE,{"derivedFrom":sQuery(id+"F40.wireOp",EDGE,"E91.2.0.0")}),-1.0]])]});
            var Q3;
            Q3=makeQuery(id+"F40.imprint","IMPRINT",FACE,{"disambiguationData":[TD([[makeQuery(id+"F40.imprint","IMPRINT",EDGE,{"derivedFrom":sQuery(id+"F40.wireOp",EDGE,"E91.3.0.0")}),-1.0]])]});
            var Q4;
            Q4=makeQuery(id+"F40.imprint","IMPRINT",FACE,{"disambiguationData":[TD([[makeQuery(id+"F40.imprint","IMPRINT",EDGE,{"derivedFrom":sQuery(id+"F40.wireOp",EDGE,"E91.4.0.0")}),-1.0]])]});
            extrude(context, id + "F41", {"entities" : qUnion([Q0, Q1, Q2, Q3, Q4]), "operationType" : NewBodyOperationType.ADD, "endBound" : BoundingType.UP_TO_NEXT, "depth" : 25 * mm});
        }
    });
